# Revit family: 1000_Sliding_Window_XX_Standard
name_source: partatom
category: Windows
revit_build: Autodesk Revit 2014 (Build: 20130308_1515(x64)
units: mm (PartAtom-declared; Revit-internal decimal feet)

## types (117) — shared parameters
Centered In Wall = Yes
Default Sill Height = 800 mm
Description = Sliding window, XX
Equal Sash Width = Yes
Frame Thickness = 76 mm
Limit Sash Height Max = 1800 mm  [stored 5.90551 ft]
Limit Sash Height Min = 300 mm
Limit Sash Width Max = 1500 mm  [stored 4.92126 ft]
Limit Sash Width Min = 300 mm
Limit Window Height Max = 1857 mm
Limit Window Height Min = 357 mm
Limit Window Width Max = 2999 mm
Limit Window Width Min = 599 mm
Manufacturer = Crealco
Model = 1000
Sash Frame Seal = 2 mm  [stored 0.00656168 ft]
URL = http://www.crealco.co.za
Wall Closure = By host
zero-valued in all types: Custom Frame Offset From Exterior, Custom Sash Width Left

## per-type parameters (varying)
- 1000SW-0906XX-1000Pa: Area Left Sash Glazing=0.15 m²; Area Right Sash Glazing=0.15 m²; Clearvue SHGC Value=0.536; Clearvue U Value=5.91; Custom Windload=1000 mm  [stored 3.28084 ft]; Custom Window Height=590 mm  [stored 1.9357 ft]; Custom Window Width=890 mm  [stored 2.91995 ft]; Energy Advantage SHGC Value=0.481; Energy Advantage U Value=4.85; Heavy Duty Interlocker=No; Height=590 mm  [stored 1.9357 ft]; Intruderprufe LowE SHGC Value=0.444; Intruderprufe LowE U Value=4.814; Intruderprufe SHGC Value=0.509; Intruderprufe U Value=5.8; Is Heavy Duty Mullion=0 mm  [stored 0 ft]; Limit Sash Width Left Max=591 mm; Limit Sash Width Left Min=300 mm; Max Pane Area=0.15 m²; Sash Height=533 mm; Sash Width Left=446 mm; Sash Width Right=446 mm; Standard Interlocker=Yes; Width=890 mm  [stored 2.91995 ft]; Windload Design=1000 mm  [stored 3.28084 ft]
- 1000SW-1206XX-1000Pa: Area Left Sash Glazing=0.21 m²; Area Right Sash Glazing=0.21 m²; Clearvue SHGC Value=0.627; Clearvue U Value=5.85; Custom Windload=1000 mm  [stored 3.28084 ft]; Custom Window Height=590 mm  [stored 1.9357 ft]; Custom Window Width=1190 mm  [stored 3.9042 ft]; Energy Advantage SHGC Value=0.562; Energy Advantage U Value=4.52; Heavy Duty Interlocker=No; Height=590 mm  [stored 1.9357 ft]; Intruderprufe LowE SHGC Value=0.525; Intruderprufe LowE U Value=4.47; Intruderprufe SHGC Value=0.595; Intruderprufe U Value=5.91; Is Heavy Duty Mullion=0 mm  [stored 0 ft]; Limit Sash Width Left Max=891 mm; Limit Sash Width Left Min=300 mm; Max Pane Area=0.21 m²; Sash Height=533 mm; Sash Width Left=596 mm; Sash Width Right=596 mm; Standard Interlocker=Yes; Width=1190 mm  [stored 3.9042 ft]; Windload Design=1000 mm  [stored 3.28084 ft]
- 1000SW-1506XX-1000Pa: Area Left Sash Glazing=0.28 m²; Area Right Sash Glazing=0.28 m²; Clearvue SHGC Value=0.568; Clearvue U Value=6.09; Custom Windload=1000 mm  [stored 3.28084 ft]; Custom Window Height=590 mm  [stored 1.9357 ft]; Custom Window Width=1490 mm  [stored 4.88845 ft]; Energy Advantage SHGC Value=0.509; Energy Advantage U Value=4.84; Heavy Duty Interlocker=No; Height=590 mm  [stored 1.9357 ft]; Intruderprufe LowE SHGC Value=0.459; Intruderprufe LowE U Value=4.81; Intruderprufe SHGC Value=0.539; Intruderprufe U Value=5.98; Is Heavy Duty Mullion=0 mm  [stored 0 ft]; Limit Sash Width Left Max=1191 mm; Limit Sash Width Left Min=300 mm; Max Pane Area=0.28 m²; Sash Height=533 mm; Sash Width Left=746 mm; Sash Width Right=746 mm; Standard Interlocker=Yes; Width=1490 mm  [stored 4.88845 ft]; Windload Design=1000 mm  [stored 3.28084 ft]
- 1000SW-1806XX-1000Pa: Area Left Sash Glazing=0.34 m²; Area Right Sash Glazing=0.34 m²; Clearvue SHGC Value=0.576; Clearvue U Value=6.14; Custom Windload=1000 mm  [stored 3.28084 ft]; Custom Window Height=590 mm  [stored 1.9357 ft]; Custom Window Width=1790 mm  [stored 5.8727 ft]; Energy Advantage SHGC Value=0.516; Energy Advantage U Value=4.84; Heavy Duty Interlocker=No; Height=590 mm  [stored 1.9357 ft]; Intruderprufe LowE SHGC Value=0.476; Intruderprufe LowE U Value=4.81; Intruderprufe SHGC Value=0.547; Intruderprufe U Value=6.02; Is Heavy Duty Mullion=0 mm  [stored 0 ft]; Limit Sash Width Left Max=1491 mm; Limit Sash Width Left Min=300 mm; Max Pane Area=0.34 m²; Sash Height=533 mm; Sash Width Left=896 mm; Sash Width Right=896 mm; Standard Interlocker=Yes; Width=1790 mm  [stored 5.8727 ft]; Windload Design=1000 mm  [stored 3.28084 ft]
- 1000SW-2106XX-1000Pa: Area Left Sash Glazing=0.41 m²; Area Right Sash Glazing=0.41 m²; Clearvue SHGC Value=0.581; Clearvue U Value=6.17; Custom Windload=1000 mm  [stored 3.28084 ft]; Custom Window Height=590 mm  [stored 1.9357 ft]; Custom Window Width=2090 mm  [stored 6.85696 ft]; Energy Advantage SHGC Value=0.521; Energy Advantage U Value=4.84; Heavy Duty Interlocker=No; Height=590 mm  [stored 1.9357 ft]; Intruderprufe LowE SHGC Value=0.48; Intruderprufe LowE U Value=4.8; Intruderprufe SHGC Value=0.552; Intruderprufe U Value=6.05; Is Heavy Duty Mullion=0 mm  [stored 0 ft]; Limit Sash Width Left Max=1500 mm  [stored 4.92126 ft]; Limit Sash Width Left Min=591 mm; Max Pane Area=0.41 m²; Sash Height=533 mm; Sash Width Left=1046 mm; Sash Width Right=1046 mm; Standard Interlocker=Yes; Width=2090 mm  [stored 6.85696 ft]; Windload Design=1000 mm  [stored 3.28084 ft]
- 1000SW-2406XX-1000Pa: Area Left Sash Glazing=0.47 m²; Area Right Sash Glazing=0.47 m²; Clearvue SHGC Value=0.586; Clearvue U Value=6.19; Custom Windload=1000 mm  [stored 3.28084 ft]; Custom Window Height=590 mm  [stored 1.9357 ft]; Custom Window Width=2390 mm  [stored 7.84121 ft]; Energy Advantage SHGC Value=0.525; Energy Advantage U Value=4.84; Heavy Duty Interlocker=No; Height=590 mm  [stored 1.9357 ft]; Intruderprufe LowE SHGC Value=0.484; Intruderprufe LowE U Value=4.8; Intruderprufe SHGC Value=0.556; Intruderprufe U Value=6.08; Is Heavy Duty Mullion=0 mm  [stored 0 ft]; Limit Sash Width Left Max=1500 mm  [stored 4.92126 ft]; Limit Sash Width Left Min=891 mm; Max Pane Area=0.47 m²; Sash Height=533 mm; Sash Width Left=1196 mm; Sash Width Right=1196 mm; Standard Interlocker=Yes; Width=2390 mm  [stored 7.84121 ft]; Windload Design=1000 mm  [stored 3.28084 ft]
- 1000SW-2706XX-1000Pa: Area Left Sash Glazing=0.54 m²; Area Right Sash Glazing=0.54 m²; Clearvue SHGC Value=0.589; Clearvue U Value=6.21; Custom Windload=1000 mm  [stored 3.28084 ft]; Custom Window Height=590 mm  [stored 1.9357 ft]; Custom Window Width=2690 mm; Energy Advantage SHGC Value=0.528; Energy Advantage U Value=4.84; Heavy Duty Interlocker=No; Height=590 mm  [stored 1.9357 ft]; Intruderprufe LowE SHGC Value=0.486; Intruderprufe LowE U Value=4.8; Intruderprufe SHGC Value=0.559; Intruderprufe U Value=6.09; Is Heavy Duty Mullion=0 mm  [stored 0 ft]; Limit Sash Width Left Max=1500 mm  [stored 4.92126 ft]; Limit Sash Width Left Min=1191 mm; Max Pane Area=0.54 m²; Sash Height=533 mm; Sash Width Left=1346 mm; Sash Width Right=1346 mm; Standard Interlocker=Yes; Width=2690 mm; Windload Design=1000 mm  [stored 3.28084 ft]
- 1000SW-3006XX-1000Pa: Area Left Sash Glazing=0.6 m²; Area Right Sash Glazing=0.6 m²; Clearvue SHGC Value=0.592; Clearvue U Value=6.22; Custom Windload=1000 mm  [stored 3.28084 ft]; Custom Window Height=590 mm  [stored 1.9357 ft]; Custom Window Width=2990 mm  [stored 9.80971 ft]; Energy Advantage SHGC Value=0.53; Energy Advantage U Value=4.84; Heavy Duty Interlocker=No; Height=590 mm  [stored 1.9357 ft]; Intruderprufe LowE SHGC Value=0.488; Intruderprufe LowE U Value=4.8; Intruderprufe SHGC Value=0.562; Intruderprufe U Value=6.11; Is Heavy Duty Mullion=0 mm  [stored 0 ft]; Limit Sash Width Left Max=1500 mm  [stored 4.92126 ft]; Limit Sash Width Left Min=1491 mm; Max Pane Area=0.6 m²; Sash Height=533 mm; Sash Width Left=1496 mm; Sash Width Right=1496 mm; Standard Interlocker=Yes; Width=2990 mm  [stored 9.80971 ft]; Windload Design=1000 mm  [stored 3.28084 ft]
- 1000SW-0909XX-1000Pa: Area Left Sash Glazing=0.25 m²; Area Right Sash Glazing=0.25 m²; Clearvue SHGC Value=0.604; Clearvue U Value=5.73; Custom Windload=1000 mm  [stored 3.28084 ft]; Custom Window Height=890 mm  [stored 2.91995 ft]; Custom Window Width=890 mm  [stored 2.91995 ft]; Energy Advantage SHGC Value=0.541; Energy Advantage U Value=4.54; Heavy Duty Interlocker=No; Height=890 mm  [stored 2.91995 ft]; Intruderprufe LowE SHGC Value=0.502; Intruderprufe LowE U Value=4.49; Intruderprufe SHGC Value=0.574; Intruderprufe U Value=5.63; Is Heavy Duty Mullion=0 mm  [stored 0 ft]; Limit Sash Width Left Max=591 mm; Limit Sash Width Left Min=300 mm; Max Pane Area=0.25 m²; Sash Height=833 mm; Sash Width Left=446 mm; Sash Width Right=446 mm; Standard Interlocker=Yes; Width=890 mm  [stored 2.91995 ft]; Windload Design=1000 mm  [stored 3.28084 ft]
- 1000SW-1209XX-1000Pa: Area Left Sash Glazing=0.36 m²; Area Right Sash Glazing=0.36 m²; Clearvue SHGC Value=0.627; Clearvue U Value=5.85; Custom Windload=1000 mm  [stored 3.28084 ft]; Custom Window Height=890 mm  [stored 2.91995 ft]; Custom Window Width=1190 mm  [stored 3.9042 ft]; Energy Advantage SHGC Value=0.562; Energy Advantage U Value=4.52; Heavy Duty Interlocker=No; Height=890 mm  [stored 2.91995 ft]; Intruderprufe LowE SHGC Value=0.52; Intruderprufe LowE U Value=4.47; Intruderprufe SHGC Value=0.595; Intruderprufe U Value=5.74; Is Heavy Duty Mullion=0 mm  [stored 0 ft]; Limit Sash Width Left Max=891 mm; Limit Sash Width Left Min=300 mm; Max Pane Area=0.36 m²; Sash Height=833 mm; Sash Width Left=596 mm; Sash Width Right=596 mm; Standard Interlocker=Yes; Width=1190 mm  [stored 3.9042 ft]; Windload Design=1000 mm  [stored 3.28084 ft]
- 1000SW-1509XX-1000Pa: Area Left Sash Glazing=0.47 m²; Area Right Sash Glazing=0.47 m²; Clearvue SHGC Value=0.641; Clearvue U Value=5.92; Custom Windload=1000 mm  [stored 3.28084 ft]; Custom Window Height=890 mm  [stored 2.91995 ft]; Custom Window Width=1490 mm  [stored 4.88845 ft]; Energy Advantage SHGC Value=0.573; Energy Advantage U Value=4.5; Heavy Duty Interlocker=No; Height=890 mm  [stored 2.91995 ft]; Intruderprufe LowE SHGC Value=0.531; Intruderprufe LowE U Value=4.45; Intruderprufe SHGC Value=0.608; Intruderprufe U Value=5.81; Is Heavy Duty Mullion=0 mm  [stored 0 ft]; Limit Sash Width Left Max=1191 mm; Limit Sash Width Left Min=300 mm; Max Pane Area=0.47 m²; Sash Height=833 mm; Sash Width Left=746 mm; Sash Width Right=746 mm; Standard Interlocker=Yes; Width=1490 mm  [stored 4.88845 ft]; Windload Design=1000 mm  [stored 3.28084 ft]
- 1000SW-1809XX-1000Pa: Area Left Sash Glazing=0.58 m²; Area Right Sash Glazing=0.58 m²; Clearvue SHGC Value=0.65; Clearvue U Value=5.97; Custom Windload=1000 mm  [stored 3.28084 ft]; Custom Window Height=890 mm  [stored 2.91995 ft]; Custom Window Width=1790 mm  [stored 5.8727 ft]; Energy Advantage SHGC Value=0.581; Energy Advantage U Value=4.5; Heavy Duty Interlocker=No; Height=890 mm  [stored 2.91995 ft]; Intruderprufe LowE SHGC Value=0.538; Intruderprufe LowE U Value=4.45; Intruderprufe SHGC Value=0.617; Intruderprufe U Value=5.85; Is Heavy Duty Mullion=0 mm  [stored 0 ft]; Limit Sash Width Left Max=1491 mm; Limit Sash Width Left Min=300 mm; Max Pane Area=0.58 m²; Sash Height=833 mm; Sash Width Left=896 mm; Sash Width Right=896 mm; Standard Interlocker=Yes; Width=1790 mm  [stored 5.8727 ft]; Windload Design=1000 mm  [stored 3.28084 ft]
- 1000SW-2109XX-1000Pa: Area Left Sash Glazing=0.69 m²; Area Right Sash Glazing=0.69 m²; Clearvue SHGC Value=0.656; Clearvue U Value=6; Custom Windload=1000 mm  [stored 3.28084 ft]; Custom Window Height=890 mm  [stored 2.91995 ft]; Custom Window Width=2090 mm  [stored 6.85696 ft]; Energy Advantage SHGC Value=0.587; Energy Advantage U Value=4.49; Heavy Duty Interlocker=No; Height=890 mm  [stored 2.91995 ft]; Intruderprufe LowE SHGC Value=0.543; Intruderprufe LowE U Value=4.44; Intruderprufe SHGC Value=0.623; Intruderprufe U Value=5.88; Is Heavy Duty Mullion=0 mm  [stored 0 ft]; Limit Sash Width Left Max=1500 mm  [stored 4.92126 ft]; Limit Sash Width Left Min=591 mm; Max Pane Area=0.69 m²; Sash Height=833 mm; Sash Width Left=1046 mm; Sash Width Right=1046 mm; Standard Interlocker=Yes; Width=2090 mm  [stored 6.85696 ft]; Windload Design=1000 mm  [stored 3.28084 ft]
- 1000SW-2409XX-1000Pa: Area Left Sash Glazing=0.8 m²; Area Right Sash Glazing=0.8 m²; Clearvue SHGC Value=0.661; Clearvue U Value=6.02; Custom Windload=1000 mm  [stored 3.28084 ft]; Custom Window Height=890 mm  [stored 2.91995 ft]; Custom Window Width=2390 mm  [stored 7.84121 ft]; Energy Advantage SHGC Value=0.591; Energy Advantage U Value=4.48; Heavy Duty Interlocker=No; Height=890 mm  [stored 2.91995 ft]; Intruderprufe LowE SHGC Value=0.547; Intruderprufe LowE U Value=4.44; Intruderprufe SHGC Value=0.627; Intruderprufe U Value=5.91; Is Heavy Duty Mullion=0 mm  [stored 0 ft]; Limit Sash Width Left Max=1500 mm  [stored 4.92126 ft]; Limit Sash Width Left Min=891 mm; Max Pane Area=0.8 m²; Sash Height=833 mm; Sash Width Left=1196 mm; Sash Width Right=1196 mm; Standard Interlocker=Yes; Width=2390 mm  [stored 7.84121 ft]; Windload Design=1000 mm  [stored 3.28084 ft]
- 1000SW-2709XX-1000Pa: Area Left Sash Glazing=0.91 m²; Area Right Sash Glazing=0.91 m²; Clearvue SHGC Value=0.665; Clearvue U Value=6.04; Custom Windload=1000 mm  [stored 3.28084 ft]; Custom Window Height=890 mm  [stored 2.91995 ft]; Custom Window Width=2690 mm; Energy Advantage SHGC Value=0.595; Energy Advantage U Value=4.48; Heavy Duty Interlocker=No; Height=890 mm  [stored 2.91995 ft]; Intruderprufe LowE SHGC Value=0.55; Intruderprufe LowE U Value=4.43; Intruderprufe SHGC Value=0.631; Intruderprufe U Value=5.92; Is Heavy Duty Mullion=0 mm  [stored 0 ft]; Limit Sash Width Left Max=1500 mm  [stored 4.92126 ft]; Limit Sash Width Left Min=1191 mm; Max Pane Area=0.91 m²; Sash Height=833 mm; Sash Width Left=1346 mm; Sash Width Right=1346 mm; Standard Interlocker=Yes; Width=2690 mm; Windload Design=1000 mm  [stored 3.28084 ft]
- 1000SW-3009XX-1000Pa: Area Left Sash Glazing=1.02 m²; Area Right Sash Glazing=1.02 m²; Clearvue SHGC Value=0.668; Clearvue U Value=6.06; Custom Windload=1000 mm  [stored 3.28084 ft]; Custom Window Height=890 mm  [stored 2.91995 ft]; Custom Window Width=2990 mm  [stored 9.80971 ft]; Energy Advantage SHGC Value=0.597; Energy Advantage U Value=4.48; Heavy Duty Interlocker=No; Height=890 mm  [stored 2.91995 ft]; Intruderprufe LowE SHGC Value=0.552; Intruderprufe LowE U Value=4.43; Intruderprufe SHGC Value=0.634; Intruderprufe U Value=5.94; Is Heavy Duty Mullion=0 mm  [stored 0 ft]; Limit Sash Width Left Max=1500 mm  [stored 4.92126 ft]; Limit Sash Width Left Min=1491 mm; Max Pane Area=1.02 m²; Sash Height=833 mm; Sash Width Left=1496 mm; Sash Width Right=1496 mm; Standard Interlocker=Yes; Width=2990 mm  [stored 9.80971 ft]; Windload Design=1000 mm  [stored 3.28084 ft]
- 1000SW-0912XX-1000Pa: Area Left Sash Glazing=0.36 m²; Area Right Sash Glazing=0.36 m²; Clearvue SHGC Value=2.638; Clearvue U Value=5.65; Custom Windload=1000 mm  [stored 3.28084 ft]; Custom Window Height=1190 mm  [stored 3.9042 ft]; Custom Window Width=890 mm  [stored 2.91995 ft]; Energy Advantage SHGC Value=0.572; Energy Advantage U Value=4.39; Heavy Duty Interlocker=No; Height=1190 mm  [stored 3.9042 ft]; Intruderprufe LowE SHGC Value=0.531; Intruderprufe LowE U Value=4.33; Intruderprufe SHGC Value=0.606; Intruderprufe U Value=5.54; Is Heavy Duty Mullion=0 mm  [stored 0 ft]; Limit Sash Width Left Max=591 mm; Limit Sash Width Left Min=300 mm; Max Pane Area=0.36 m²; Sash Height=1133 mm; Sash Width Left=446 mm; Sash Width Right=446 mm; Standard Interlocker=Yes; Width=890 mm  [stored 2.91995 ft]; Windload Design=1000 mm  [stored 3.28084 ft]
- 1000SW-1212XX-1000Pa: Area Left Sash Glazing=0.51 m²; Area Right Sash Glazing=0.51 m²; Clearvue SHGC Value=0.662; Clearvue U Value=5.77; Custom Windload=1000 mm  [stored 3.28084 ft]; Custom Window Height=1190 mm  [stored 3.9042 ft]; Custom Window Width=1190 mm  [stored 3.9042 ft]; Energy Advantage SHGC Value=0.593; Energy Advantage U Value=4.35; Heavy Duty Interlocker=No; Height=1190 mm  [stored 3.9042 ft]; Intruderprufe LowE SHGC Value=0.55; Intruderprufe LowE U Value=4.3; Intruderprufe SHGC Value=0.629; Intruderprufe U Value=5.65; Is Heavy Duty Mullion=0 mm  [stored 0 ft]; Limit Sash Width Left Max=891 mm; Limit Sash Width Left Min=300 mm; Max Pane Area=0.51 m²; Sash Height=1133 mm; Sash Width Left=596 mm; Sash Width Right=596 mm; Standard Interlocker=Yes; Width=1190 mm  [stored 3.9042 ft]; Windload Design=1000 mm  [stored 3.28084 ft]
- 1000SW-1512XX-1000Pa: Area Left Sash Glazing=0.67 m²; Area Right Sash Glazing=0.67 m²; Clearvue SHGC Value=0.677; Clearvue U Value=5.84; Custom Windload=1000 mm  [stored 3.28084 ft]; Custom Window Height=1190 mm  [stored 3.9042 ft]; Custom Window Width=1490 mm  [stored 4.88845 ft]; Energy Advantage SHGC Value=0.605; Energy Advantage U Value=4.34; Heavy Duty Interlocker=No; Height=1190 mm  [stored 3.9042 ft]; Intruderprufe LowE SHGC Value=0.561; Intruderprufe LowE U Value=4.28; Intruderprufe SHGC Value=0.642; Intruderprufe U Value=5.72; Is Heavy Duty Mullion=0 mm  [stored 0 ft]; Limit Sash Width Left Max=1191 mm; Limit Sash Width Left Min=300 mm; Max Pane Area=0.67 m²; Sash Height=1133 mm; Sash Width Left=746 mm; Sash Width Right=746 mm; Standard Interlocker=Yes; Width=1490 mm  [stored 4.88845 ft]; Windload Design=1000 mm  [stored 3.28084 ft]
- 1000SW-1812XX-1000Pa: Area Left Sash Glazing=0.82 m²; Area Right Sash Glazing=0.82 m²; Clearvue SHGC Value=0.686; Clearvue U Value=5.88; Custom Windload=1000 mm  [stored 3.28084 ft]; Custom Window Height=1190 mm  [stored 3.9042 ft]; Custom Window Width=1790 mm  [stored 5.8727 ft]; Energy Advantage SHGC Value=0.614; Energy Advantage U Value=4.32; Heavy Duty Interlocker=No; Height=1190 mm  [stored 3.9042 ft]; Intruderprufe LowE SHGC Value=0.569; Intruderprufe LowE U Value=4.27; Intruderprufe SHGC Value=0.651; Intruderprufe U Value=5.77; Is Heavy Duty Mullion=0 mm  [stored 0 ft]; Limit Sash Width Left Max=1491 mm; Limit Sash Width Left Min=300 mm; Max Pane Area=0.82 m²; Sash Height=1133 mm; Sash Width Left=896 mm; Sash Width Right=896 mm; Standard Interlocker=Yes; Width=1790 mm  [stored 5.8727 ft]; Windload Design=1000 mm  [stored 3.28084 ft]
- 1000SW-2112XX-1000Pa: Area Left Sash Glazing=0.98 m²; Area Right Sash Glazing=0.98 m²; Clearvue SHGC Value=0.693; Clearvue U Value=5.92; Custom Windload=1000 mm  [stored 3.28084 ft]; Custom Window Height=1190 mm  [stored 3.9042 ft]; Custom Window Width=2090 mm  [stored 6.85696 ft]; Energy Advantage SHGC Value=0.62; Energy Advantage U Value=4.32; Heavy Duty Interlocker=No; Height=1190 mm  [stored 3.9042 ft]; Intruderprufe LowE SHGC Value=0.574; Intruderprufe LowE U Value=4.26; Intruderprufe SHGC Value=0.658; Intruderprufe U Value=5.8; Is Heavy Duty Mullion=0 mm  [stored 0 ft]; Limit Sash Width Left Max=1500 mm  [stored 4.92126 ft]; Limit Sash Width Left Min=591 mm; Max Pane Area=0.98 m²; Sash Height=1133 mm; Sash Width Left=1046 mm; Sash Width Right=1046 mm; Standard Interlocker=Yes; Width=2090 mm  [stored 6.85696 ft]; Windload Design=1000 mm  [stored 3.28084 ft]
- 1000SW-2412XX-1000Pa: Area Left Sash Glazing=1.13 m²; Area Right Sash Glazing=1.13 m²; Clearvue SHGC Value=0.698; Clearvue U Value=5.94; Custom Windload=1000 mm  [stored 3.28084 ft]; Custom Window Height=1190 mm  [stored 3.9042 ft]; Custom Window Width=2390 mm  [stored 7.84121 ft]; Energy Advantage SHGC Value=0.624; Energy Advantage U Value=4.31; Heavy Duty Interlocker=No; Height=1190 mm  [stored 3.9042 ft]; Intruderprufe LowE SHGC Value=0.578; Intruderprufe LowE U Value=4.26; Intruderprufe SHGC Value=0.663; Intruderprufe U Value=5.82; Is Heavy Duty Mullion=0 mm  [stored 0 ft]; Limit Sash Width Left Max=1500 mm  [stored 4.92126 ft]; Limit Sash Width Left Min=891 mm; Max Pane Area=1.13 m²; Sash Height=1133 mm; Sash Width Left=1196 mm; Sash Width Right=1196 mm; Standard Interlocker=Yes; Width=2390 mm  [stored 7.84121 ft]; Windload Design=1000 mm  [stored 3.28084 ft]
- 1000SW-2712XX-1000Pa: Area Left Sash Glazing=1.28 m²; Area Right Sash Glazing=1.28 m²; Clearvue SHGC Value=0.702; Clearvue U Value=5.96; Custom Windload=1000 mm  [stored 3.28084 ft]; Custom Window Height=1190 mm  [stored 3.9042 ft]; Custom Window Width=2690 mm; Energy Advantage SHGC Value=0.628; Energy Advantage U Value=4.3; Heavy Duty Interlocker=No; Height=1190 mm  [stored 3.9042 ft]; Intruderprufe LowE SHGC Value=0.582; Intruderprufe LowE U Value=4.25; Intruderprufe SHGC Value=0.666; Intruderprufe U Value=5.84; Is Heavy Duty Mullion=0 mm  [stored 0 ft]; Limit Sash Width Left Max=1500 mm  [stored 4.92126 ft]; Limit Sash Width Left Min=1191 mm; Max Pane Area=1.28 m²; Sash Height=1133 mm; Sash Width Left=1346 mm; Sash Width Right=1346 mm; Standard Interlocker=Yes; Width=2690 mm; Windload Design=1000 mm  [stored 3.28084 ft]
- 1000SW-3012XX-1000Pa: Area Left Sash Glazing=1.44 m²; Area Right Sash Glazing=1.44 m²; Clearvue SHGC Value=0.705; Clearvue U Value=5.98; Custom Windload=1000 mm  [stored 3.28084 ft]; Custom Window Height=1190 mm  [stored 3.9042 ft]; Custom Window Width=2990 mm  [stored 9.80971 ft]; Energy Advantage SHGC Value=0.631; Energy Advantage U Value=4.3; Heavy Duty Interlocker=No; Height=1190 mm  [stored 3.9042 ft]; Intruderprufe LowE SHGC Value=0.584; Intruderprufe LowE U Value=4.25; Intruderprufe SHGC Value=0.669; Intruderprufe U Value=5.86; Is Heavy Duty Mullion=0 mm  [stored 0 ft]; Limit Sash Width Left Max=1500 mm  [stored 4.92126 ft]; Limit Sash Width Left Min=1491 mm; Max Pane Area=1.44 m²; Sash Height=1133 mm; Sash Width Left=1496 mm; Sash Width Right=1496 mm; Standard Interlocker=Yes; Width=2990 mm  [stored 9.80971 ft]; Windload Design=1000 mm  [stored 3.28084 ft]
- 1000SW-0915XX-1000Pa: Area Left Sash Glazing=0.46 m²; Area Right Sash Glazing=0.46 m²; Clearvue SHGC Value=0.658; Clearvue U Value=5.6; Custom Windload=1000 mm  [stored 3.28084 ft]; Custom Window Height=1490 mm  [stored 4.88845 ft]; Custom Window Width=890 mm  [stored 2.91995 ft]; Energy Advantage SHGC Value=0.59; Energy Advantage U Value=4.29; Heavy Duty Interlocker=No; Height=1490 mm  [stored 4.88845 ft]; Intruderprufe LowE SHGC Value=0.548; Intruderprufe LowE U Value=4.23; Intruderprufe SHGC Value=0.625; Intruderprufe U Value=5.49; Is Heavy Duty Mullion=0 mm  [stored 0 ft]; Limit Sash Width Left Max=591 mm; Limit Sash Width Left Min=300 mm; Max Pane Area=0.46 m²; Sash Height=1433 mm; Sash Width Left=446 mm; Sash Width Right=446 mm; Standard Interlocker=Yes; Width=890 mm  [stored 2.91995 ft]; Windload Design=1000 mm  [stored 3.28084 ft]
- 1000SW-1215XX-1000Pa: Area Left Sash Glazing=0.66 m²; Area Right Sash Glazing=0.66 m²; Clearvue SHGC Value=0.683; Clearvue U Value=5.72; Custom Windload=1000 mm  [stored 3.28084 ft]; Custom Window Height=1490 mm  [stored 4.88845 ft]; Custom Window Width=1190 mm  [stored 3.9042 ft]; Energy Advantage SHGC Value=0.611; Energy Advantage U Value=4.26; Heavy Duty Interlocker=No; Height=1490 mm  [stored 4.88845 ft]; Intruderprufe LowE SHGC Value=0.568; Intruderprufe LowE U Value=4.2; Intruderprufe SHGC Value=0.649; Intruderprufe U Value=5.6; Is Heavy Duty Mullion=0 mm  [stored 0 ft]; Limit Sash Width Left Max=891 mm; Limit Sash Width Left Min=300 mm; Max Pane Area=0.66 m²; Sash Height=1433 mm; Sash Width Left=596 mm; Sash Width Right=596 mm; Standard Interlocker=Yes; Width=1190 mm  [stored 3.9042 ft]; Windload Design=1000 mm  [stored 3.28084 ft]
- 1000SW-1515XX-1000Pa: Area Left Sash Glazing=0.86 m²; Area Right Sash Glazing=0.86 m²; Clearvue SHGC Value=0.698; Clearvue U Value=5.79; Custom Windload=1000 mm  [stored 3.28084 ft]; Custom Window Height=1490 mm  [stored 4.88845 ft]; Custom Window Width=1490 mm  [stored 4.88845 ft]; Energy Advantage SHGC Value=0.625; Energy Advantage U Value=4.24; Heavy Duty Interlocker=No; Height=1490 mm  [stored 4.88845 ft]; Intruderprufe LowE SHGC Value=0.58; Intruderprufe LowE U Value=4.18; Intruderprufe SHGC Value=0.663; Intruderprufe U Value=5.67; Is Heavy Duty Mullion=0 mm  [stored 0 ft]; Limit Sash Width Left Max=1191 mm; Limit Sash Width Left Min=300 mm; Max Pane Area=0.86 m²; Sash Height=1433 mm; Sash Width Left=746 mm; Sash Width Right=746 mm; Standard Interlocker=Yes; Width=1490 mm  [stored 4.88845 ft]; Windload Design=1000 mm  [stored 3.28084 ft]
- 1000SW-1815XX-1000Pa: Area Left Sash Glazing=1.06 m²; Area Right Sash Glazing=1.06 m²; Clearvue SHGC Value=0.708; Clearvue U Value=5.83; Custom Windload=1000 mm  [stored 3.28084 ft]; Custom Window Height=1490 mm  [stored 4.88845 ft]; Custom Window Width=1790 mm  [stored 5.8727 ft]; Energy Advantage SHGC Value=0.633; Energy Advantage U Value=4.22; Heavy Duty Interlocker=No; Height=1490 mm  [stored 4.88845 ft]; Intruderprufe LowE SHGC Value=0.587; Intruderprufe LowE U Value=4.16; Intruderprufe SHGC Value=0.672; Intruderprufe U Value=5.72; Is Heavy Duty Mullion=0 mm  [stored 0 ft]; Limit Sash Width Left Max=1491 mm; Limit Sash Width Left Min=300 mm; Max Pane Area=1.06 m²; Sash Height=1433 mm; Sash Width Left=896 mm; Sash Width Right=896 mm; Standard Interlocker=Yes; Width=1790 mm  [stored 5.8727 ft]; Windload Design=1000 mm  [stored 3.28084 ft]
- 1000SW-2115XX-1000Pa: Area Left Sash Glazing=1.26 m²; Area Right Sash Glazing=1.26 m²; Clearvue SHGC Value=0.715; Clearvue U Value=5.87; Custom Windload=1000 mm  [stored 3.28084 ft]; Custom Window Height=1490 mm  [stored 4.88845 ft]; Custom Window Width=2090 mm  [stored 6.85696 ft]; Energy Advantage SHGC Value=0.639; Energy Advantage U Value=4.21; Heavy Duty Interlocker=No; Height=1490 mm  [stored 4.88845 ft]; Intruderprufe LowE SHGC Value=0.595; Intruderprufe LowE U Value=4.15; Intruderprufe SHGC Value=0.679; Intruderprufe U Value=5.75; Is Heavy Duty Mullion=0 mm  [stored 0 ft]; Limit Sash Width Left Max=1500 mm  [stored 4.92126 ft]; Limit Sash Width Left Min=591 mm; Max Pane Area=1.26 m²; Sash Height=1433 mm; Sash Width Left=1046 mm; Sash Width Right=1046 mm; Standard Interlocker=Yes; Width=2090 mm  [stored 6.85696 ft]; Windload Design=1000 mm  [stored 3.28084 ft]
- 1000SW-2415XX-1000Pa: Area Left Sash Glazing=1.46 m²; Area Right Sash Glazing=1.46 m²; Clearvue SHGC Value=0.721; Clearvue U Value=5.89; Custom Windload=1000 mm  [stored 3.28084 ft]; Custom Window Height=1490 mm  [stored 4.88845 ft]; Custom Window Width=2390 mm  [stored 7.84121 ft]; Energy Advantage SHGC Value=0.644; Energy Advantage U Value=4.2; Heavy Duty Interlocker=No; Height=1490 mm  [stored 4.88845 ft]; Intruderprufe LowE SHGC Value=0.597; Intruderprufe LowE U Value=4.15; Intruderprufe SHGC Value=0.684; Intruderprufe U Value=5.77; Is Heavy Duty Mullion=0 mm  [stored 0 ft]; Limit Sash Width Left Max=1500 mm  [stored 4.92126 ft]; Limit Sash Width Left Min=891 mm; Max Pane Area=1.46 m²; Sash Height=1433 mm; Sash Width Left=1196 mm; Sash Width Right=1196 mm; Standard Interlocker=Yes; Width=2390 mm  [stored 7.84121 ft]; Windload Design=1000 mm  [stored 3.28084 ft]
- 1000SW-2715XX-1000Pa: Area Left Sash Glazing=1.66 m²; Area Right Sash Glazing=1.66 m²; Clearvue SHGC Value=0.725; Clearvue U Value=5.91; Custom Windload=1000 mm  [stored 3.28084 ft]; Custom Window Height=1490 mm  [stored 4.88845 ft]; Custom Window Width=2690 mm; Energy Advantage SHGC Value=0.648; Energy Advantage U Value=4.2; Heavy Duty Interlocker=No; Height=1490 mm  [stored 4.88845 ft]; Intruderprufe LowE SHGC Value=0.601; Intruderprufe LowE U Value=4.14; Intruderprufe SHGC Value=0.687; Intruderprufe U Value=5.79; Is Heavy Duty Mullion=0 mm  [stored 0 ft]; Limit Sash Width Left Max=1500 mm  [stored 4.92126 ft]; Limit Sash Width Left Min=1191 mm; Max Pane Area=1.66 m²; Sash Height=1433 mm; Sash Width Left=1346 mm; Sash Width Right=1346 mm; Standard Interlocker=Yes; Width=2690 mm; Windload Design=1000 mm  [stored 3.28084 ft]
- 1000SW-3015XX-1000Pa: Area Left Sash Glazing=1.86 m²; Area Right Sash Glazing=1.86 m²; Clearvue SHGC Value=0.728; Clearvue U Value=5.93; Custom Windload=1000 mm  [stored 3.28084 ft]; Custom Window Height=1490 mm  [stored 4.88845 ft]; Custom Window Width=2990 mm  [stored 9.80971 ft]; Energy Advantage SHGC Value=0.651; Energy Advantage U Value=4.19; Heavy Duty Interlocker=No; Height=1490 mm  [stored 4.88845 ft]; Intruderprufe LowE SHGC Value=0.603; Intruderprufe LowE U Value=4.14; Intruderprufe SHGC Value=0.691; Intruderprufe U Value=5.81; Is Heavy Duty Mullion=0 mm  [stored 0 ft]; Limit Sash Width Left Max=1500 mm  [stored 4.92126 ft]; Limit Sash Width Left Min=1491 mm; Max Pane Area=1.86 m²; Sash Height=1433 mm; Sash Width Left=1496 mm; Sash Width Right=1496 mm; Standard Interlocker=Yes; Width=2990 mm  [stored 9.80971 ft]; Windload Design=1000 mm  [stored 3.28084 ft]
- 1000SW-1218XX-1000Pa: Area Left Sash Glazing=0.81 m²; Area Right Sash Glazing=0.81 m²; Clearvue SHGC Value=0.697; Clearvue U Value=5.68; Custom Windload=1000 mm  [stored 3.28084 ft]; Custom Window Height=1790 mm  [stored 5.8727 ft]; Custom Window Width=1190 mm  [stored 3.9042 ft]; Energy Advantage SHGC Value=0.624; Energy Advantage U Value=4.19; Heavy Duty Interlocker=No; Height=1790 mm  [stored 5.8727 ft]; Intruderprufe LowE SHGC Value=0.579; Intruderprufe LowE U Value=4.13; Intruderprufe SHGC Value=0.662; Intruderprufe U Value=5.57; Is Heavy Duty Mullion=0 mm  [stored 0 ft]; Limit Sash Width Left Max=891 mm; Limit Sash Width Left Min=300 mm; Max Pane Area=0.81 m²; Sash Height=1733 mm; Sash Width Left=596 mm; Sash Width Right=596 mm; Standard Interlocker=Yes; Width=1190 mm  [stored 3.9042 ft]; Windload Design=1000 mm  [stored 3.28084 ft]
- 1000SW-1518XX-1000Pa: Area Left Sash Glazing=1.05 m²; Area Right Sash Glazing=1.05 m²; Clearvue SHGC Value=0.713; Clearvue U Value=5.75; Custom Windload=1000 mm  [stored 3.28084 ft]; Custom Window Height=1790 mm  [stored 5.8727 ft]; Custom Window Width=1490 mm  [stored 4.88845 ft]; Energy Advantage SHGC Value=0.637; Energy Advantage U Value=4.17; Heavy Duty Interlocker=Yes; Height=1790 mm  [stored 5.8727 ft]; Intruderprufe LowE SHGC Value=0.592; Intruderprufe LowE U Value=4.11; Intruderprufe SHGC Value=0.676; Intruderprufe U Value=5.64; Is Heavy Duty Mullion=1 mm  [stored 0.00328084 ft]; Limit Sash Width Left Max=1191 mm; Limit Sash Width Left Min=300 mm; Max Pane Area=1.05 m²; Sash Height=1733 mm; Sash Width Left=746 mm; Sash Width Right=746 mm; Standard Interlocker=No; Width=1490 mm  [stored 4.88845 ft]; Windload Design=1000 mm  [stored 3.28084 ft]
- 1000SW-1818XX-1000Pa: Area Left Sash Glazing=1.3 m²; Area Right Sash Glazing=1.3 m²; Clearvue SHGC Value=0.723; Clearvue U Value=5.8; Custom Windload=1000 mm  [stored 3.28084 ft]; Custom Window Height=1790 mm  [stored 5.8727 ft]; Custom Window Width=1790 mm  [stored 5.8727 ft]; Energy Advantage SHGC Value=0.646; Energy Advantage U Value=4.15; Heavy Duty Interlocker=Yes; Height=1790 mm  [stored 5.8727 ft]; Intruderprufe LowE SHGC Value=0.6; Intruderprufe LowE U Value=4.09; Intruderprufe SHGC Value=0.686; Intruderprufe U Value=5.68; Is Heavy Duty Mullion=1 mm  [stored 0.00328084 ft]; Limit Sash Width Left Max=1491 mm; Limit Sash Width Left Min=300 mm; Max Pane Area=1.3 m²; Sash Height=1733 mm; Sash Width Left=896 mm; Sash Width Right=896 mm; Standard Interlocker=No; Width=1790 mm  [stored 5.8727 ft]; Windload Design=1000 mm  [stored 3.28084 ft]
- 1000SW-2118XX-1000Pa: Area Left Sash Glazing=1.54 m²; Area Right Sash Glazing=1.54 m²; Clearvue SHGC Value=0.73; Clearvue U Value=5.83; Custom Windload=1000 mm  [stored 3.28084 ft]; Custom Window Height=1790 mm  [stored 5.8727 ft]; Custom Window Width=2090 mm  [stored 6.85696 ft]; Energy Advantage SHGC Value=0.652; Energy Advantage U Value=4.14; Heavy Duty Interlocker=Yes; Height=1790 mm  [stored 5.8727 ft]; Intruderprufe LowE SHGC Value=0.605; Intruderprufe LowE U Value=4.08; Intruderprufe SHGC Value=0.693; Intruderprufe U Value=5.71; Is Heavy Duty Mullion=1 mm  [stored 0.00328084 ft]; Limit Sash Width Left Max=1500 mm  [stored 4.92126 ft]; Limit Sash Width Left Min=591 mm; Max Pane Area=1.54 m²; Sash Height=1733 mm; Sash Width Left=1046 mm; Sash Width Right=1046 mm; Standard Interlocker=No; Width=2090 mm  [stored 6.85696 ft]; Windload Design=1000 mm  [stored 3.28084 ft]
- 1000SW-2418XX-1000Pa: Area Left Sash Glazing=1.79 m²; Area Right Sash Glazing=1.79 m²; Clearvue SHGC Value=0.735; Clearvue U Value=5.86; Custom Windload=1000 mm  [stored 3.28084 ft]; Custom Window Height=1790 mm  [stored 5.8727 ft]; Custom Window Width=2390 mm  [stored 7.84121 ft]; Energy Advantage SHGC Value=0.657; Energy Advantage U Value=4.13; Heavy Duty Interlocker=Yes; Height=1790 mm  [stored 5.8727 ft]; Intruderprufe LowE SHGC Value=0.61; Intruderprufe LowE U Value=4.07; Intruderprufe SHGC Value=0.698; Intruderprufe U Value=5.74; Is Heavy Duty Mullion=1 mm  [stored 0.00328084 ft]; Limit Sash Width Left Max=1500 mm  [stored 4.92126 ft]; Limit Sash Width Left Min=891 mm; Max Pane Area=1.79 m²; Sash Height=1733 mm; Sash Width Left=1196 mm; Sash Width Right=1196 mm; Standard Interlocker=No; Width=2390 mm  [stored 7.84121 ft]; Windload Design=1000 mm  [stored 3.28084 ft]
- 1000SW-2718XX-1000Pa: Area Left Sash Glazing=2.03 m²; Area Right Sash Glazing=2.03 m²; Clearvue SHGC Value=0.74; Clearvue U Value=5.88; Custom Windload=1000 mm  [stored 3.28084 ft]; Custom Window Height=1790 mm  [stored 5.8727 ft]; Custom Window Width=2690 mm; Energy Advantage SHGC Value=0.661; Energy Advantage U Value=4.13; Heavy Duty Interlocker=Yes; Height=1790 mm  [stored 5.8727 ft]; Intruderprufe LowE SHGC Value=0.613; Intruderprufe LowE U Value=4.07; Intruderprufe SHGC Value=0.702; Intruderprufe U Value=5.76; Is Heavy Duty Mullion=1 mm  [stored 0.00328084 ft]; Limit Sash Width Left Max=1500 mm  [stored 4.92126 ft]; Limit Sash Width Left Min=1191 mm; Max Pane Area=2.03 m²; Sash Height=1733 mm; Sash Width Left=1346 mm; Sash Width Right=1346 mm; Standard Interlocker=No; Width=2690 mm; Windload Design=1000 mm  [stored 3.28084 ft]
- 1000SW-3018XX-1000Pa: Area Left Sash Glazing=2.28 m²; Area Right Sash Glazing=2.28 m²; Clearvue SHGC Value=0.743; Clearvue U Value=5.9; Custom Windload=1000 mm  [stored 3.28084 ft]; Custom Window Height=1790 mm  [stored 5.8727 ft]; Custom Window Width=2990 mm  [stored 9.80971 ft]; Energy Advantage SHGC Value=0.664; Energy Advantage U Value=4.12; Heavy Duty Interlocker=Yes; Height=1790 mm  [stored 5.8727 ft]; Intruderprufe LowE SHGC Value=0.616; Intruderprufe LowE U Value=4.06; Intruderprufe SHGC Value=0.705; Intruderprufe U Value=5.77; Is Heavy Duty Mullion=1 mm  [stored 0.00328084 ft]; Limit Sash Width Left Max=1500 mm  [stored 4.92126 ft]; Limit Sash Width Left Min=1491 mm; Max Pane Area=2.28 m²; Sash Height=1733 mm; Sash Width Left=1496 mm; Sash Width Right=1496 mm; Standard Interlocker=No; Width=2990 mm  [stored 9.80971 ft]; Windload Design=1000 mm  [stored 3.28084 ft]
- 1000SW-0906XX-1500Pa: Area Left Sash Glazing=0.15 m²; Area Right Sash Glazing=0.15 m²; Clearvue SHGC Value=0.536; Clearvue U Value=5.91; Custom Windload=1500 mm  [stored 4.92126 ft]; Custom Window Height=590 mm  [stored 1.9357 ft]; Custom Window Width=890 mm  [stored 2.91995 ft]; Energy Advantage SHGC Value=0.481; Energy Advantage U Value=4.85; Heavy Duty Interlocker=No; Height=590 mm  [stored 1.9357 ft]; Intruderprufe LowE SHGC Value=0.444; Intruderprufe LowE U Value=4.814; Intruderprufe SHGC Value=0.509; Intruderprufe U Value=5.8; Is Heavy Duty Mullion=0 mm  [stored 0 ft]; Limit Sash Width Left Max=591 mm; Limit Sash Width Left Min=300 mm; Max Pane Area=0.15 m²; Sash Height=533 mm; Sash Width Left=446 mm; Sash Width Right=446 mm; Standard Interlocker=Yes; Width=890 mm  [stored 2.91995 ft]; Windload Design=1500 mm  [stored 4.92126 ft]
- 1000SW-0906XX-2000Pa: Area Left Sash Glazing=0.15 m²; Area Right Sash Glazing=0.15 m²; Clearvue SHGC Value=0.536; Clearvue U Value=5.91; Custom Windload=2000 mm  [stored 6.56168 ft]; Custom Window Height=590 mm  [stored 1.9357 ft]; Custom Window Width=890 mm  [stored 2.91995 ft]; Energy Advantage SHGC Value=0.481; Energy Advantage U Value=4.85; Heavy Duty Interlocker=No; Height=590 mm  [stored 1.9357 ft]; Intruderprufe LowE SHGC Value=0.444; Intruderprufe LowE U Value=4.814; Intruderprufe SHGC Value=0.509; Intruderprufe U Value=5.8; Is Heavy Duty Mullion=0 mm  [stored 0 ft]; Limit Sash Width Left Max=591 mm; Limit Sash Width Left Min=300 mm; Max Pane Area=0.15 m²; Sash Height=533 mm; Sash Width Left=446 mm; Sash Width Right=446 mm; Standard Interlocker=Yes; Width=890 mm  [stored 2.91995 ft]; Windload Design=2000 mm  [stored 6.56168 ft]
- 1000SW-0909XX-1500Pa: Area Left Sash Glazing=0.25 m²; Area Right Sash Glazing=0.25 m²; Clearvue SHGC Value=0.604; Clearvue U Value=5.73; Custom Windload=1500 mm  [stored 4.92126 ft]; Custom Window Height=890 mm  [stored 2.91995 ft]; Custom Window Width=890 mm  [stored 2.91995 ft]; Energy Advantage SHGC Value=0.541; Energy Advantage U Value=4.54; Heavy Duty Interlocker=No; Height=890 mm  [stored 2.91995 ft]; Intruderprufe LowE SHGC Value=0.502; Intruderprufe LowE U Value=4.49; Intruderprufe SHGC Value=0.574; Intruderprufe U Value=5.63; Is Heavy Duty Mullion=0 mm  [stored 0 ft]; Limit Sash Width Left Max=591 mm; Limit Sash Width Left Min=300 mm; Max Pane Area=0.25 m²; Sash Height=833 mm; Sash Width Left=446 mm; Sash Width Right=446 mm; Standard Interlocker=Yes; Width=890 mm  [stored 2.91995 ft]; Windload Design=1500 mm  [stored 4.92126 ft]
- 1000SW-0909XX-2000Pa: Area Left Sash Glazing=0.25 m²; Area Right Sash Glazing=0.25 m²; Clearvue SHGC Value=0.604; Clearvue U Value=5.73; Custom Windload=2000 mm  [stored 6.56168 ft]; Custom Window Height=890 mm  [stored 2.91995 ft]; Custom Window Width=890 mm  [stored 2.91995 ft]; Energy Advantage SHGC Value=0.541; Energy Advantage U Value=4.54; Heavy Duty Interlocker=No; Height=890 mm  [stored 2.91995 ft]; Intruderprufe LowE SHGC Value=0.502; Intruderprufe LowE U Value=4.49; Intruderprufe SHGC Value=0.574; Intruderprufe U Value=5.63; Is Heavy Duty Mullion=0 mm  [stored 0 ft]; Limit Sash Width Left Max=591 mm; Limit Sash Width Left Min=300 mm; Max Pane Area=0.25 m²; Sash Height=833 mm; Sash Width Left=446 mm; Sash Width Right=446 mm; Standard Interlocker=Yes; Width=890 mm  [stored 2.91995 ft]; Windload Design=2000 mm  [stored 6.56168 ft]
- 1000SW-0912XX-1500Pa: Area Left Sash Glazing=0.36 m²; Area Right Sash Glazing=0.36 m²; Clearvue SHGC Value=2.638; Clearvue U Value=5.65; Custom Windload=1500 mm  [stored 4.92126 ft]; Custom Window Height=1190 mm  [stored 3.9042 ft]; Custom Window Width=890 mm  [stored 2.91995 ft]; Energy Advantage SHGC Value=0.572; Energy Advantage U Value=4.39; Heavy Duty Interlocker=No; Height=1190 mm  [stored 3.9042 ft]; Intruderprufe LowE SHGC Value=0.531; Intruderprufe LowE U Value=4.33; Intruderprufe SHGC Value=0.606; Intruderprufe U Value=5.54; Is Heavy Duty Mullion=0 mm  [stored 0 ft]; Limit Sash Width Left Max=591 mm; Limit Sash Width Left Min=300 mm; Max Pane Area=0.36 m²; Sash Height=1133 mm; Sash Width Left=446 mm; Sash Width Right=446 mm; Standard Interlocker=Yes; Width=890 mm  [stored 2.91995 ft]; Windload Design=1500 mm  [stored 4.92126 ft]
- 1000SW-0912XX-2000Pa: Area Left Sash Glazing=0.36 m²; Area Right Sash Glazing=0.36 m²; Clearvue SHGC Value=2.638; Clearvue U Value=5.65; Custom Windload=2000 mm  [stored 6.56168 ft]; Custom Window Height=1190 mm  [stored 3.9042 ft]; Custom Window Width=890 mm  [stored 2.91995 ft]; Energy Advantage SHGC Value=0.572; Energy Advantage U Value=4.39; Heavy Duty Interlocker=No; Height=1190 mm  [stored 3.9042 ft]; Intruderprufe LowE SHGC Value=0.531; Intruderprufe LowE U Value=4.33; Intruderprufe SHGC Value=0.606; Intruderprufe U Value=5.54; Is Heavy Duty Mullion=0 mm  [stored 0 ft]; Limit Sash Width Left Max=591 mm; Limit Sash Width Left Min=300 mm; Max Pane Area=0.36 m²; Sash Height=1133 mm; Sash Width Left=446 mm; Sash Width Right=446 mm; Standard Interlocker=Yes; Width=890 mm  [stored 2.91995 ft]; Windload Design=2000 mm  [stored 6.56168 ft]
- 1000SW-0915XX-1500Pa: Area Left Sash Glazing=0.46 m²; Area Right Sash Glazing=0.46 m²; Clearvue SHGC Value=0.658; Clearvue U Value=5.6; Custom Windload=1500 mm  [stored 4.92126 ft]; Custom Window Height=1490 mm  [stored 4.88845 ft]; Custom Window Width=890 mm  [stored 2.91995 ft]; Energy Advantage SHGC Value=0.59; Energy Advantage U Value=4.29; Heavy Duty Interlocker=No; Height=1490 mm  [stored 4.88845 ft]; Intruderprufe LowE SHGC Value=0.548; Intruderprufe LowE U Value=4.23; Intruderprufe SHGC Value=0.625; Intruderprufe U Value=5.49; Is Heavy Duty Mullion=0 mm  [stored 0 ft]; Limit Sash Width Left Max=591 mm; Limit Sash Width Left Min=300 mm; Max Pane Area=0.46 m²; Sash Height=1433 mm; Sash Width Left=446 mm; Sash Width Right=446 mm; Standard Interlocker=Yes; Width=890 mm  [stored 2.91995 ft]; Windload Design=1500 mm  [stored 4.92126 ft]
- 1000SW-0915XX-2000Pa: Area Left Sash Glazing=0.46 m²; Area Right Sash Glazing=0.46 m²; Clearvue SHGC Value=0.658; Clearvue U Value=5.6; Custom Windload=2000 mm  [stored 6.56168 ft]; Custom Window Height=1490 mm  [stored 4.88845 ft]; Custom Window Width=890 mm  [stored 2.91995 ft]; Energy Advantage SHGC Value=0.59; Energy Advantage U Value=4.29; Heavy Duty Interlocker=No; Height=1490 mm  [stored 4.88845 ft]; Intruderprufe LowE SHGC Value=0.548; Intruderprufe LowE U Value=4.23; Intruderprufe SHGC Value=0.625; Intruderprufe U Value=5.49; Is Heavy Duty Mullion=0 mm  [stored 0 ft]; Limit Sash Width Left Max=591 mm; Limit Sash Width Left Min=300 mm; Max Pane Area=0.46 m²; Sash Height=1433 mm; Sash Width Left=446 mm; Sash Width Right=446 mm; Standard Interlocker=Yes; Width=890 mm  [stored 2.91995 ft]; Windload Design=2000 mm  [stored 6.56168 ft]
- 1000SW-1206XX-1500Pa: Area Left Sash Glazing=0.21 m²; Area Right Sash Glazing=0.21 m²; Clearvue SHGC Value=0.627; Clearvue U Value=5.85; Custom Windload=1500 mm  [stored 4.92126 ft]; Custom Window Height=590 mm  [stored 1.9357 ft]; Custom Window Width=1190 mm  [stored 3.9042 ft]; Energy Advantage SHGC Value=0.562; Energy Advantage U Value=4.52; Heavy Duty Interlocker=No; Height=590 mm  [stored 1.9357 ft]; Intruderprufe LowE SHGC Value=0.525; Intruderprufe LowE U Value=4.47; Intruderprufe SHGC Value=0.595; Intruderprufe U Value=5.91; Is Heavy Duty Mullion=0 mm  [stored 0 ft]; Limit Sash Width Left Max=891 mm; Limit Sash Width Left Min=300 mm; Max Pane Area=0.21 m²; Sash Height=533 mm; Sash Width Left=596 mm; Sash Width Right=596 mm; Standard Interlocker=Yes; Width=1190 mm  [stored 3.9042 ft]; Windload Design=1500 mm  [stored 4.92126 ft]
- 1000SW-1206XX-2000Pa: Area Left Sash Glazing=0.21 m²; Area Right Sash Glazing=0.21 m²; Clearvue SHGC Value=0.627; Clearvue U Value=5.85; Custom Windload=2000 mm  [stored 6.56168 ft]; Custom Window Height=590 mm  [stored 1.9357 ft]; Custom Window Width=1190 mm  [stored 3.9042 ft]; Energy Advantage SHGC Value=0.562; Energy Advantage U Value=4.52; Heavy Duty Interlocker=No; Height=590 mm  [stored 1.9357 ft]; Intruderprufe LowE SHGC Value=0.525; Intruderprufe LowE U Value=4.47; Intruderprufe SHGC Value=0.595; Intruderprufe U Value=5.91; Is Heavy Duty Mullion=0 mm  [stored 0 ft]; Limit Sash Width Left Max=891 mm; Limit Sash Width Left Min=300 mm; Max Pane Area=0.21 m²; Sash Height=533 mm; Sash Width Left=596 mm; Sash Width Right=596 mm; Standard Interlocker=Yes; Width=1190 mm  [stored 3.9042 ft]; Windload Design=2000 mm  [stored 6.56168 ft]
- 1000SW-1209XX-1500Pa: Area Left Sash Glazing=0.36 m²; Area Right Sash Glazing=0.36 m²; Clearvue SHGC Value=0.627; Clearvue U Value=5.85; Custom Windload=1500 mm  [stored 4.92126 ft]; Custom Window Height=890 mm  [stored 2.91995 ft]; Custom Window Width=1190 mm  [stored 3.9042 ft]; Energy Advantage SHGC Value=0.562; Energy Advantage U Value=4.52; Heavy Duty Interlocker=No; Height=890 mm  [stored 2.91995 ft]; Intruderprufe LowE SHGC Value=0.52; Intruderprufe LowE U Value=4.47; Intruderprufe SHGC Value=0.595; Intruderprufe U Value=5.74; Is Heavy Duty Mullion=0 mm  [stored 0 ft]; Limit Sash Width Left Max=891 mm; Limit Sash Width Left Min=300 mm; Max Pane Area=0.36 m²; Sash Height=833 mm; Sash Width Left=596 mm; Sash Width Right=596 mm; Standard Interlocker=Yes; Width=1190 mm  [stored 3.9042 ft]; Windload Design=1500 mm  [stored 4.92126 ft]
- 1000SW-1209XX-2000Pa: Area Left Sash Glazing=0.36 m²; Area Right Sash Glazing=0.36 m²; Clearvue SHGC Value=0.627; Clearvue U Value=5.85; Custom Windload=2000 mm  [stored 6.56168 ft]; Custom Window Height=890 mm  [stored 2.91995 ft]; Custom Window Width=1190 mm  [stored 3.9042 ft]; Energy Advantage SHGC Value=0.562; Energy Advantage U Value=4.52; Heavy Duty Interlocker=No; Height=890 mm  [stored 2.91995 ft]; Intruderprufe LowE SHGC Value=0.52; Intruderprufe LowE U Value=4.47; Intruderprufe SHGC Value=0.595; Intruderprufe U Value=5.74; Is Heavy Duty Mullion=0 mm  [stored 0 ft]; Limit Sash Width Left Max=891 mm; Limit Sash Width Left Min=300 mm; Max Pane Area=0.36 m²; Sash Height=833 mm; Sash Width Left=596 mm; Sash Width Right=596 mm; Standard Interlocker=Yes; Width=1190 mm  [stored 3.9042 ft]; Windload Design=2000 mm  [stored 6.56168 ft]
- 1000SW-1212XX-1500Pa: Area Left Sash Glazing=0.51 m²; Area Right Sash Glazing=0.51 m²; Clearvue SHGC Value=0.662; Clearvue U Value=5.77; Custom Windload=1500 mm  [stored 4.92126 ft]; Custom Window Height=1190 mm  [stored 3.9042 ft]; Custom Window Width=1190 mm  [stored 3.9042 ft]; Energy Advantage SHGC Value=0.593; Energy Advantage U Value=4.35; Heavy Duty Interlocker=No; Height=1190 mm  [stored 3.9042 ft]; Intruderprufe LowE SHGC Value=0.55; Intruderprufe LowE U Value=4.3; Intruderprufe SHGC Value=0.629; Intruderprufe U Value=5.65; Is Heavy Duty Mullion=0 mm  [stored 0 ft]; Limit Sash Width Left Max=891 mm; Limit Sash Width Left Min=300 mm; Max Pane Area=0.51 m²; Sash Height=1133 mm; Sash Width Left=596 mm; Sash Width Right=596 mm; Standard Interlocker=Yes; Width=1190 mm  [stored 3.9042 ft]; Windload Design=1500 mm  [stored 4.92126 ft]
- 1000SW-1212XX-2000Pa: Area Left Sash Glazing=0.51 m²; Area Right Sash Glazing=0.51 m²; Clearvue SHGC Value=0.662; Clearvue U Value=5.77; Custom Windload=2000 mm  [stored 6.56168 ft]; Custom Window Height=1190 mm  [stored 3.9042 ft]; Custom Window Width=1190 mm  [stored 3.9042 ft]; Energy Advantage SHGC Value=0.593; Energy Advantage U Value=4.35; Heavy Duty Interlocker=No; Height=1190 mm  [stored 3.9042 ft]; Intruderprufe LowE SHGC Value=0.55; Intruderprufe LowE U Value=4.3; Intruderprufe SHGC Value=0.629; Intruderprufe U Value=5.65; Is Heavy Duty Mullion=0 mm  [stored 0 ft]; Limit Sash Width Left Max=891 mm; Limit Sash Width Left Min=300 mm; Max Pane Area=0.51 m²; Sash Height=1133 mm; Sash Width Left=596 mm; Sash Width Right=596 mm; Standard Interlocker=Yes; Width=1190 mm  [stored 3.9042 ft]; Windload Design=2000 mm  [stored 6.56168 ft]
- 1000SW-1215XX-1500Pa: Area Left Sash Glazing=0.66 m²; Area Right Sash Glazing=0.66 m²; Clearvue SHGC Value=0.683; Clearvue U Value=5.72; Custom Windload=1500 mm  [stored 4.92126 ft]; Custom Window Height=1490 mm  [stored 4.88845 ft]; Custom Window Width=1190 mm  [stored 3.9042 ft]; Energy Advantage SHGC Value=0.611; Energy Advantage U Value=4.26; Heavy Duty Interlocker=No; Height=1490 mm  [stored 4.88845 ft]; Intruderprufe LowE SHGC Value=0.568; Intruderprufe LowE U Value=4.2; Intruderprufe SHGC Value=0.649; Intruderprufe U Value=5.6; Is Heavy Duty Mullion=0 mm  [stored 0 ft]; Limit Sash Width Left Max=891 mm; Limit Sash Width Left Min=300 mm; Max Pane Area=0.66 m²; Sash Height=1433 mm; Sash Width Left=596 mm; Sash Width Right=596 mm; Standard Interlocker=Yes; Width=1190 mm  [stored 3.9042 ft]; Windload Design=1500 mm  [stored 4.92126 ft]
- 1000SW-1215XX-2000Pa: Area Left Sash Glazing=0.66 m²; Area Right Sash Glazing=0.66 m²; Clearvue SHGC Value=0.683; Clearvue U Value=5.72; Custom Windload=2000 mm  [stored 6.56168 ft]; Custom Window Height=1490 mm  [stored 4.88845 ft]; Custom Window Width=1190 mm  [stored 3.9042 ft]; Energy Advantage SHGC Value=0.611; Energy Advantage U Value=4.26; Heavy Duty Interlocker=No; Height=1490 mm  [stored 4.88845 ft]; Intruderprufe LowE SHGC Value=0.568; Intruderprufe LowE U Value=4.2; Intruderprufe SHGC Value=0.649; Intruderprufe U Value=5.6; Is Heavy Duty Mullion=0 mm  [stored 0 ft]; Limit Sash Width Left Max=891 mm; Limit Sash Width Left Min=300 mm; Max Pane Area=0.66 m²; Sash Height=1433 mm; Sash Width Left=596 mm; Sash Width Right=596 mm; Standard Interlocker=Yes; Width=1190 mm  [stored 3.9042 ft]; Windload Design=2000 mm  [stored 6.56168 ft]
- 1000SW-1218XX-1500Pa: Area Left Sash Glazing=0.81 m²; Area Right Sash Glazing=0.81 m²; Clearvue SHGC Value=0.697; Clearvue U Value=5.68; Custom Windload=1500 mm  [stored 4.92126 ft]; Custom Window Height=1790 mm  [stored 5.8727 ft]; Custom Window Width=1190 mm  [stored 3.9042 ft]; Energy Advantage SHGC Value=0.624; Energy Advantage U Value=4.19; Heavy Duty Interlocker=Yes; Height=1790 mm  [stored 5.8727 ft]; Intruderprufe LowE SHGC Value=0.579; Intruderprufe LowE U Value=4.13; Intruderprufe SHGC Value=0.662; Intruderprufe U Value=5.57; Is Heavy Duty Mullion=1 mm  [stored 0.00328084 ft]; Limit Sash Width Left Max=891 mm; Limit Sash Width Left Min=300 mm; Max Pane Area=0.81 m²; Sash Height=1733 mm; Sash Width Left=596 mm; Sash Width Right=596 mm; Standard Interlocker=No; Width=1190 mm  [stored 3.9042 ft]; Windload Design=1500 mm  [stored 4.92126 ft]
- 1000SW-1218XX-2000Pa: Area Left Sash Glazing=0.81 m²; Area Right Sash Glazing=0.81 m²; Clearvue SHGC Value=0.697; Clearvue U Value=5.68; Custom Windload=2000 mm  [stored 6.56168 ft]; Custom Window Height=1790 mm  [stored 5.8727 ft]; Custom Window Width=1190 mm  [stored 3.9042 ft]; Energy Advantage SHGC Value=0.624; Energy Advantage U Value=4.19; Heavy Duty Interlocker=Yes; Height=1790 mm  [stored 5.8727 ft]; Intruderprufe LowE SHGC Value=0.579; Intruderprufe LowE U Value=4.13; Intruderprufe SHGC Value=0.662; Intruderprufe U Value=5.57; Is Heavy Duty Mullion=1 mm  [stored 0.00328084 ft]; Limit Sash Width Left Max=891 mm; Limit Sash Width Left Min=300 mm; Max Pane Area=0.81 m²; Sash Height=1733 mm; Sash Width Left=596 mm; Sash Width Right=596 mm; Standard Interlocker=No; Width=1190 mm  [stored 3.9042 ft]; Windload Design=2000 mm  [stored 6.56168 ft]
- 1000SW-1506XX-1500Pa: Area Left Sash Glazing=0.28 m²; Area Right Sash Glazing=0.28 m²; Clearvue SHGC Value=0.568; Clearvue U Value=6.09; Custom Windload=1500 mm  [stored 4.92126 ft]; Custom Window Height=590 mm  [stored 1.9357 ft]; Custom Window Width=1490 mm  [stored 4.88845 ft]; Energy Advantage SHGC Value=0.509; Energy Advantage U Value=4.84; Heavy Duty Interlocker=No; Height=590 mm  [stored 1.9357 ft]; Intruderprufe LowE SHGC Value=0.459; Intruderprufe LowE U Value=4.81; Intruderprufe SHGC Value=0.539; Intruderprufe U Value=5.98; Is Heavy Duty Mullion=0 mm  [stored 0 ft]; Limit Sash Width Left Max=1191 mm; Limit Sash Width Left Min=300 mm; Max Pane Area=0.28 m²; Sash Height=533 mm; Sash Width Left=746 mm; Sash Width Right=746 mm; Standard Interlocker=Yes; Width=1490 mm  [stored 4.88845 ft]; Windload Design=1500 mm  [stored 4.92126 ft]
- 1000SW-1506XX-2000Pa: Area Left Sash Glazing=0.28 m²; Area Right Sash Glazing=0.28 m²; Clearvue SHGC Value=0.568; Clearvue U Value=6.09; Custom Windload=2000 mm  [stored 6.56168 ft]; Custom Window Height=590 mm  [stored 1.9357 ft]; Custom Window Width=1490 mm  [stored 4.88845 ft]; Energy Advantage SHGC Value=0.509; Energy Advantage U Value=4.84; Heavy Duty Interlocker=No; Height=590 mm  [stored 1.9357 ft]; Intruderprufe LowE SHGC Value=0.459; Intruderprufe LowE U Value=4.81; Intruderprufe SHGC Value=0.539; Intruderprufe U Value=5.98; Is Heavy Duty Mullion=0 mm  [stored 0 ft]; Limit Sash Width Left Max=1191 mm; Limit Sash Width Left Min=300 mm; Max Pane Area=0.28 m²; Sash Height=533 mm; Sash Width Left=746 mm; Sash Width Right=746 mm; Standard Interlocker=Yes; Width=1490 mm  [stored 4.88845 ft]; Windload Design=2000 mm  [stored 6.56168 ft]
- 1000SW-1509XX-1500Pa: Area Left Sash Glazing=0.47 m²; Area Right Sash Glazing=0.47 m²; Clearvue SHGC Value=0.641; Clearvue U Value=5.92; Custom Windload=1500 mm  [stored 4.92126 ft]; Custom Window Height=890 mm  [stored 2.91995 ft]; Custom Window Width=1490 mm  [stored 4.88845 ft]; Energy Advantage SHGC Value=0.573; Energy Advantage U Value=4.5; Heavy Duty Interlocker=No; Height=890 mm  [stored 2.91995 ft]; Intruderprufe LowE SHGC Value=0.531; Intruderprufe LowE U Value=4.45; Intruderprufe SHGC Value=0.608; Intruderprufe U Value=5.81; Is Heavy Duty Mullion=0 mm  [stored 0 ft]; Limit Sash Width Left Max=1191 mm; Limit Sash Width Left Min=300 mm; Max Pane Area=0.47 m²; Sash Height=833 mm; Sash Width Left=746 mm; Sash Width Right=746 mm; Standard Interlocker=Yes; Width=1490 mm  [stored 4.88845 ft]; Windload Design=1500 mm  [stored 4.92126 ft]
- 1000SW-1509XX-2000Pa: Area Left Sash Glazing=0.47 m²; Area Right Sash Glazing=0.47 m²; Clearvue SHGC Value=0.641; Clearvue U Value=5.92; Custom Windload=2000 mm  [stored 6.56168 ft]; Custom Window Height=890 mm  [stored 2.91995 ft]; Custom Window Width=1490 mm  [stored 4.88845 ft]; Energy Advantage SHGC Value=0.573; Energy Advantage U Value=4.5; Heavy Duty Interlocker=No; Height=890 mm  [stored 2.91995 ft]; Intruderprufe LowE SHGC Value=0.531; Intruderprufe LowE U Value=4.45; Intruderprufe SHGC Value=0.608; Intruderprufe U Value=5.81; Is Heavy Duty Mullion=0 mm  [stored 0 ft]; Limit Sash Width Left Max=1191 mm; Limit Sash Width Left Min=300 mm; Max Pane Area=0.47 m²; Sash Height=833 mm; Sash Width Left=746 mm; Sash Width Right=746 mm; Standard Interlocker=Yes; Width=1490 mm  [stored 4.88845 ft]; Windload Design=2000 mm  [stored 6.56168 ft]
- 1000SW-1512XX-1500Pa: Area Left Sash Glazing=0.67 m²; Area Right Sash Glazing=0.67 m²; Clearvue SHGC Value=0.677; Clearvue U Value=5.84; Custom Windload=1500 mm  [stored 4.92126 ft]; Custom Window Height=1190 mm  [stored 3.9042 ft]; Custom Window Width=1490 mm  [stored 4.88845 ft]; Energy Advantage SHGC Value=0.605; Energy Advantage U Value=4.34; Heavy Duty Interlocker=No; Height=1190 mm  [stored 3.9042 ft]; Intruderprufe LowE SHGC Value=0.561; Intruderprufe LowE U Value=4.28; Intruderprufe SHGC Value=0.642; Intruderprufe U Value=5.72; Is Heavy Duty Mullion=0 mm  [stored 0 ft]; Limit Sash Width Left Max=1191 mm; Limit Sash Width Left Min=300 mm; Max Pane Area=0.67 m²; Sash Height=1133 mm; Sash Width Left=746 mm; Sash Width Right=746 mm; Standard Interlocker=Yes; Width=1490 mm  [stored 4.88845 ft]; Windload Design=1500 mm  [stored 4.92126 ft]
- 1000SW-1512XX-2000Pa: Area Left Sash Glazing=0.67 m²; Area Right Sash Glazing=0.67 m²; Clearvue SHGC Value=0.677; Clearvue U Value=5.84; Custom Windload=2000 mm  [stored 6.56168 ft]; Custom Window Height=1190 mm  [stored 3.9042 ft]; Custom Window Width=1490 mm  [stored 4.88845 ft]; Energy Advantage SHGC Value=0.605; Energy Advantage U Value=4.34; Heavy Duty Interlocker=No; Height=1190 mm  [stored 3.9042 ft]; Intruderprufe LowE SHGC Value=0.561; Intruderprufe LowE U Value=4.28; Intruderprufe SHGC Value=0.642; Intruderprufe U Value=5.72; Is Heavy Duty Mullion=0 mm  [stored 0 ft]; Limit Sash Width Left Max=1191 mm; Limit Sash Width Left Min=300 mm; Max Pane Area=0.67 m²; Sash Height=1133 mm; Sash Width Left=746 mm; Sash Width Right=746 mm; Standard Interlocker=Yes; Width=1490 mm  [stored 4.88845 ft]; Windload Design=2000 mm  [stored 6.56168 ft]
- 1000SW-1515XX-1500Pa: Area Left Sash Glazing=0.86 m²; Area Right Sash Glazing=0.86 m²; Clearvue SHGC Value=0.698; Clearvue U Value=5.79; Custom Windload=1500 mm  [stored 4.92126 ft]; Custom Window Height=1490 mm  [stored 4.88845 ft]; Custom Window Width=1490 mm  [stored 4.88845 ft]; Energy Advantage SHGC Value=0.625; Energy Advantage U Value=4.24; Heavy Duty Interlocker=No; Height=1490 mm  [stored 4.88845 ft]; Intruderprufe LowE SHGC Value=0.58; Intruderprufe LowE U Value=4.18; Intruderprufe SHGC Value=0.663; Intruderprufe U Value=5.67; Is Heavy Duty Mullion=0 mm  [stored 0 ft]; Limit Sash Width Left Max=1191 mm; Limit Sash Width Left Min=300 mm; Max Pane Area=0.86 m²; Sash Height=1433 mm; Sash Width Left=746 mm; Sash Width Right=746 mm; Standard Interlocker=Yes; Width=1490 mm  [stored 4.88845 ft]; Windload Design=1500 mm  [stored 4.92126 ft]
- 1000SW-1515XX-2000Pa: Area Left Sash Glazing=0.86 m²; Area Right Sash Glazing=0.86 m²; Clearvue SHGC Value=0.698; Clearvue U Value=5.79; Custom Windload=2000 mm  [stored 6.56168 ft]; Custom Window Height=1490 mm  [stored 4.88845 ft]; Custom Window Width=1490 mm  [stored 4.88845 ft]; Energy Advantage SHGC Value=0.625; Energy Advantage U Value=4.24; Heavy Duty Interlocker=Yes; Height=1490 mm  [stored 4.88845 ft]; Intruderprufe LowE SHGC Value=0.58; Intruderprufe LowE U Value=4.18; Intruderprufe SHGC Value=0.663; Intruderprufe U Value=5.67; Is Heavy Duty Mullion=1 mm  [stored 0.00328084 ft]; Limit Sash Width Left Max=1191 mm; Limit Sash Width Left Min=300 mm; Max Pane Area=0.86 m²; Sash Height=1433 mm; Sash Width Left=746 mm; Sash Width Right=746 mm; Standard Interlocker=No; Width=1490 mm  [stored 4.88845 ft]; Windload Design=2000 mm  [stored 6.56168 ft]
- 1000SW-1518XX-1500Pa: Area Left Sash Glazing=1.05 m²; Area Right Sash Glazing=1.05 m²; Clearvue SHGC Value=0.713; Clearvue U Value=5.75; Custom Windload=1500 mm  [stored 4.92126 ft]; Custom Window Height=1790 mm  [stored 5.8727 ft]; Custom Window Width=1490 mm  [stored 4.88845 ft]; Energy Advantage SHGC Value=0.637; Energy Advantage U Value=4.17; Heavy Duty Interlocker=Yes; Height=1790 mm  [stored 5.8727 ft]; Intruderprufe LowE SHGC Value=0.592; Intruderprufe LowE U Value=4.11; Intruderprufe SHGC Value=0.676; Intruderprufe U Value=5.64; Is Heavy Duty Mullion=1 mm  [stored 0.00328084 ft]; Limit Sash Width Left Max=1191 mm; Limit Sash Width Left Min=300 mm; Max Pane Area=1.05 m²; Sash Height=1733 mm; Sash Width Left=746 mm; Sash Width Right=746 mm; Standard Interlocker=No; Width=1490 mm  [stored 4.88845 ft]; Windload Design=1500 mm  [stored 4.92126 ft]
- 1000SW-1518XX-2000Pa: Area Left Sash Glazing=1.05 m²; Area Right Sash Glazing=1.05 m²; Clearvue SHGC Value=0.713; Clearvue U Value=5.75; Custom Windload=2000 mm  [stored 6.56168 ft]; Custom Window Height=1790 mm  [stored 5.8727 ft]; Custom Window Width=1490 mm  [stored 4.88845 ft]; Energy Advantage SHGC Value=0.637; Energy Advantage U Value=4.17; Heavy Duty Interlocker=Yes; Height=1790 mm  [stored 5.8727 ft]; Intruderprufe LowE SHGC Value=0.592; Intruderprufe LowE U Value=4.11; Intruderprufe SHGC Value=0.676; Intruderprufe U Value=5.64; Is Heavy Duty Mullion=1 mm  [stored 0.00328084 ft]; Limit Sash Width Left Max=1191 mm; Limit Sash Width Left Min=300 mm; Max Pane Area=1.05 m²; Sash Height=1733 mm; Sash Width Left=746 mm; Sash Width Right=746 mm; Standard Interlocker=No; Width=1490 mm  [stored 4.88845 ft]; Windload Design=2000 mm  [stored 6.56168 ft]
- 1000SW-1806XX-1500Pa: Area Left Sash Glazing=0.34 m²; Area Right Sash Glazing=0.34 m²; Clearvue SHGC Value=0.576; Clearvue U Value=6.14; Custom Windload=1500 mm  [stored 4.92126 ft]; Custom Window Height=590 mm  [stored 1.9357 ft]; Custom Window Width=1790 mm  [stored 5.8727 ft]; Energy Advantage SHGC Value=0.516; Energy Advantage U Value=4.84; Heavy Duty Interlocker=No; Height=590 mm  [stored 1.9357 ft]; Intruderprufe LowE SHGC Value=0.476; Intruderprufe LowE U Value=4.81; Intruderprufe SHGC Value=0.547; Intruderprufe U Value=6.02; Is Heavy Duty Mullion=0 mm  [stored 0 ft]; Limit Sash Width Left Max=1491 mm; Limit Sash Width Left Min=300 mm; Max Pane Area=0.34 m²; Sash Height=533 mm; Sash Width Left=896 mm; Sash Width Right=896 mm; Standard Interlocker=Yes; Width=1790 mm  [stored 5.8727 ft]; Windload Design=1500 mm  [stored 4.92126 ft]
- 1000SW-1806XX-2000Pa: Area Left Sash Glazing=0.34 m²; Area Right Sash Glazing=0.34 m²; Clearvue SHGC Value=0.576; Clearvue U Value=6.14; Custom Windload=2000 mm  [stored 6.56168 ft]; Custom Window Height=590 mm  [stored 1.9357 ft]; Custom Window Width=1790 mm  [stored 5.8727 ft]; Energy Advantage SHGC Value=0.516; Energy Advantage U Value=4.84; Heavy Duty Interlocker=No; Height=590 mm  [stored 1.9357 ft]; Intruderprufe LowE SHGC Value=0.476; Intruderprufe LowE U Value=4.81; Intruderprufe SHGC Value=0.547; Intruderprufe U Value=6.02; Is Heavy Duty Mullion=0 mm  [stored 0 ft]; Limit Sash Width Left Max=1491 mm; Limit Sash Width Left Min=300 mm; Max Pane Area=0.34 m²; Sash Height=533 mm; Sash Width Left=896 mm; Sash Width Right=896 mm; Standard Interlocker=Yes; Width=1790 mm  [stored 5.8727 ft]; Windload Design=2000 mm  [stored 6.56168 ft]
- 1000SW-1809XX-1500Pa: Area Left Sash Glazing=0.58 m²; Area Right Sash Glazing=0.58 m²; Clearvue SHGC Value=0.65; Clearvue U Value=5.97; Custom Windload=1500 mm  [stored 4.92126 ft]; Custom Window Height=890 mm  [stored 2.91995 ft]; Custom Window Width=1790 mm  [stored 5.8727 ft]; Energy Advantage SHGC Value=0.581; Energy Advantage U Value=4.5; Heavy Duty Interlocker=No; Height=890 mm  [stored 2.91995 ft]; Intruderprufe LowE SHGC Value=0.538; Intruderprufe LowE U Value=4.45; Intruderprufe SHGC Value=0.617; Intruderprufe U Value=5.85; Is Heavy Duty Mullion=0 mm  [stored 0 ft]; Limit Sash Width Left Max=1491 mm; Limit Sash Width Left Min=300 mm; Max Pane Area=0.58 m²; Sash Height=833 mm; Sash Width Left=896 mm; Sash Width Right=896 mm; Standard Interlocker=Yes; Width=1790 mm  [stored 5.8727 ft]; Windload Design=1500 mm  [stored 4.92126 ft]
- 1000SW-1809XX-2000Pa: Area Left Sash Glazing=0.58 m²; Area Right Sash Glazing=0.58 m²; Clearvue SHGC Value=0.65; Clearvue U Value=5.97; Custom Windload=2000 mm  [stored 6.56168 ft]; Custom Window Height=890 mm  [stored 2.91995 ft]; Custom Window Width=1790 mm  [stored 5.8727 ft]; Energy Advantage SHGC Value=0.581; Energy Advantage U Value=4.5; Heavy Duty Interlocker=No; Height=890 mm  [stored 2.91995 ft]; Intruderprufe LowE SHGC Value=0.538; Intruderprufe LowE U Value=4.45; Intruderprufe SHGC Value=0.617; Intruderprufe U Value=5.85; Is Heavy Duty Mullion=0 mm  [stored 0 ft]; Limit Sash Width Left Max=1491 mm; Limit Sash Width Left Min=300 mm; Max Pane Area=0.58 m²; Sash Height=833 mm; Sash Width Left=896 mm; Sash Width Right=896 mm; Standard Interlocker=Yes; Width=1790 mm  [stored 5.8727 ft]; Windload Design=2000 mm  [stored 6.56168 ft]
- 1000SW-1812XX-1500Pa: Area Left Sash Glazing=0.82 m²; Area Right Sash Glazing=0.82 m²; Clearvue SHGC Value=0.686; Clearvue U Value=5.88; Custom Windload=1500 mm  [stored 4.92126 ft]; Custom Window Height=1190 mm  [stored 3.9042 ft]; Custom Window Width=1790 mm  [stored 5.8727 ft]; Energy Advantage SHGC Value=0.614; Energy Advantage U Value=4.32; Heavy Duty Interlocker=No; Height=1190 mm  [stored 3.9042 ft]; Intruderprufe LowE SHGC Value=0.569; Intruderprufe LowE U Value=4.27; Intruderprufe SHGC Value=0.651; Intruderprufe U Value=5.77; Is Heavy Duty Mullion=0 mm  [stored 0 ft]; Limit Sash Width Left Max=1491 mm; Limit Sash Width Left Min=300 mm; Max Pane Area=0.82 m²; Sash Height=1133 mm; Sash Width Left=896 mm; Sash Width Right=896 mm; Standard Interlocker=Yes; Width=1790 mm  [stored 5.8727 ft]; Windload Design=1500 mm  [stored 4.92126 ft]
- 1000SW-1812XX-2000Pa: Area Left Sash Glazing=0.82 m²; Area Right Sash Glazing=0.82 m²; Clearvue SHGC Value=0.686; Clearvue U Value=5.88; Custom Windload=2000 mm  [stored 6.56168 ft]; Custom Window Height=1190 mm  [stored 3.9042 ft]; Custom Window Width=1790 mm  [stored 5.8727 ft]; Energy Advantage SHGC Value=0.614; Energy Advantage U Value=4.32; Heavy Duty Interlocker=No; Height=1190 mm  [stored 3.9042 ft]; Intruderprufe LowE SHGC Value=0.569; Intruderprufe LowE U Value=4.27; Intruderprufe SHGC Value=0.651; Intruderprufe U Value=5.77; Is Heavy Duty Mullion=0 mm  [stored 0 ft]; Limit Sash Width Left Max=1491 mm; Limit Sash Width Left Min=300 mm; Max Pane Area=0.82 m²; Sash Height=1133 mm; Sash Width Left=896 mm; Sash Width Right=896 mm; Standard Interlocker=Yes; Width=1790 mm  [stored 5.8727 ft]; Windload Design=2000 mm  [stored 6.56168 ft]
- 1000SW-1815XX-1500Pa: Area Left Sash Glazing=1.06 m²; Area Right Sash Glazing=1.06 m²; Clearvue SHGC Value=0.708; Clearvue U Value=5.83; Custom Windload=1500 mm  [stored 4.92126 ft]; Custom Window Height=1490 mm  [stored 4.88845 ft]; Custom Window Width=1790 mm  [stored 5.8727 ft]; Energy Advantage SHGC Value=0.633; Energy Advantage U Value=4.22; Heavy Duty Interlocker=Yes; Height=1490 mm  [stored 4.88845 ft]; Intruderprufe LowE SHGC Value=0.587; Intruderprufe LowE U Value=4.16; Intruderprufe SHGC Value=0.672; Intruderprufe U Value=5.72; Is Heavy Duty Mullion=1 mm  [stored 0.00328084 ft]; Limit Sash Width Left Max=1491 mm; Limit Sash Width Left Min=300 mm; Max Pane Area=1.06 m²; Sash Height=1433 mm; Sash Width Left=896 mm; Sash Width Right=896 mm; Standard Interlocker=No; Width=1790 mm  [stored 5.8727 ft]; Windload Design=1500 mm  [stored 4.92126 ft]
- 1000SW-1815XX-2000Pa: Area Left Sash Glazing=1.06 m²; Area Right Sash Glazing=1.06 m²; Clearvue SHGC Value=0.708; Clearvue U Value=5.83; Custom Windload=2000 mm  [stored 6.56168 ft]; Custom Window Height=1490 mm  [stored 4.88845 ft]; Custom Window Width=1790 mm  [stored 5.8727 ft]; Energy Advantage SHGC Value=0.633; Energy Advantage U Value=4.22; Heavy Duty Interlocker=Yes; Height=1490 mm  [stored 4.88845 ft]; Intruderprufe LowE SHGC Value=0.587; Intruderprufe LowE U Value=4.16; Intruderprufe SHGC Value=0.672; Intruderprufe U Value=5.72; Is Heavy Duty Mullion=1 mm  [stored 0.00328084 ft]; Limit Sash Width Left Max=1491 mm; Limit Sash Width Left Min=300 mm; Max Pane Area=1.06 m²; Sash Height=1433 mm; Sash Width Left=896 mm; Sash Width Right=896 mm; Standard Interlocker=No; Width=1790 mm  [stored 5.8727 ft]; Windload Design=2000 mm  [stored 6.56168 ft]
- 1000SW-1818XX-1500Pa: Area Left Sash Glazing=1.3 m²; Area Right Sash Glazing=1.3 m²; Clearvue SHGC Value=0.723; Clearvue U Value=5.8; Custom Windload=1500 mm  [stored 4.92126 ft]; Custom Window Height=1790 mm  [stored 5.8727 ft]; Custom Window Width=1790 mm  [stored 5.8727 ft]; Energy Advantage SHGC Value=0.646; Energy Advantage U Value=4.15; Heavy Duty Interlocker=Yes; Height=1790 mm  [stored 5.8727 ft]; Intruderprufe LowE SHGC Value=0.6; Intruderprufe LowE U Value=4.09; Intruderprufe SHGC Value=0.686; Intruderprufe U Value=5.68; Is Heavy Duty Mullion=1 mm  [stored 0.00328084 ft]; Limit Sash Width Left Max=1491 mm; Limit Sash Width Left Min=300 mm; Max Pane Area=1.3 m²; Sash Height=1733 mm; Sash Width Left=896 mm; Sash Width Right=896 mm; Standard Interlocker=No; Width=1790 mm  [stored 5.8727 ft]; Windload Design=1500 mm  [stored 4.92126 ft]
- 1000SW-1818XX-2000Pa: Area Left Sash Glazing=1.3 m²; Area Right Sash Glazing=1.3 m²; Clearvue SHGC Value=0.723; Clearvue U Value=5.8; Custom Windload=2000 mm  [stored 6.56168 ft]; Custom Window Height=1790 mm  [stored 5.8727 ft]; Custom Window Width=1790 mm  [stored 5.8727 ft]; Energy Advantage SHGC Value=0.646; Energy Advantage U Value=4.15; Heavy Duty Interlocker=Yes; Height=1790 mm  [stored 5.8727 ft]; Intruderprufe LowE SHGC Value=0.6; Intruderprufe LowE U Value=4.09; Intruderprufe SHGC Value=0.686; Intruderprufe U Value=5.68; Is Heavy Duty Mullion=1 mm  [stored 0.00328084 ft]; Limit Sash Width Left Max=1491 mm; Limit Sash Width Left Min=300 mm; Max Pane Area=1.3 m²; Sash Height=1733 mm; Sash Width Left=896 mm; Sash Width Right=896 mm; Standard Interlocker=No; Width=1790 mm  [stored 5.8727 ft]; Windload Design=2000 mm  [stored 6.56168 ft]
- 1000SW-2106XX-1500Pa: Area Left Sash Glazing=0.41 m²; Area Right Sash Glazing=0.41 m²; Clearvue SHGC Value=0.581; Clearvue U Value=6.17; Custom Windload=1500 mm  [stored 4.92126 ft]; Custom Window Height=590 mm  [stored 1.9357 ft]; Custom Window Width=2090 mm  [stored 6.85696 ft]; Energy Advantage SHGC Value=0.521; Energy Advantage U Value=4.84; Heavy Duty Interlocker=No; Height=590 mm  [stored 1.9357 ft]; Intruderprufe LowE SHGC Value=0.48; Intruderprufe LowE U Value=4.8; Intruderprufe SHGC Value=0.552; Intruderprufe U Value=6.05; Is Heavy Duty Mullion=0 mm  [stored 0 ft]; Limit Sash Width Left Max=1500 mm  [stored 4.92126 ft]; Limit Sash Width Left Min=591 mm; Max Pane Area=0.41 m²; Sash Height=533 mm; Sash Width Left=1046 mm; Sash Width Right=1046 mm; Standard Interlocker=Yes; Width=2090 mm  [stored 6.85696 ft]; Windload Design=1500 mm  [stored 4.92126 ft]
- 1000SW-2106XX-2000Pa: Area Left Sash Glazing=0.41 m²; Area Right Sash Glazing=0.41 m²; Clearvue SHGC Value=0.581; Clearvue U Value=6.17; Custom Windload=2000 mm  [stored 6.56168 ft]; Custom Window Height=590 mm  [stored 1.9357 ft]; Custom Window Width=2090 mm  [stored 6.85696 ft]; Energy Advantage SHGC Value=0.521; Energy Advantage U Value=4.84; Heavy Duty Interlocker=No; Height=590 mm  [stored 1.9357 ft]; Intruderprufe LowE SHGC Value=0.48; Intruderprufe LowE U Value=4.8; Intruderprufe SHGC Value=0.552; Intruderprufe U Value=6.05; Is Heavy Duty Mullion=0 mm  [stored 0 ft]; Limit Sash Width Left Max=1500 mm  [stored 4.92126 ft]; Limit Sash Width Left Min=591 mm; Max Pane Area=0.41 m²; Sash Height=533 mm; Sash Width Left=1046 mm; Sash Width Right=1046 mm; Standard Interlocker=Yes; Width=2090 mm  [stored 6.85696 ft]; Windload Design=2000 mm  [stored 6.56168 ft]
- 1000SW-2109XX-1500Pa: Area Left Sash Glazing=0.69 m²; Area Right Sash Glazing=0.69 m²; Clearvue SHGC Value=0.656; Clearvue U Value=6; Custom Windload=1500 mm  [stored 4.92126 ft]; Custom Window Height=890 mm  [stored 2.91995 ft]; Custom Window Width=2090 mm  [stored 6.85696 ft]; Energy Advantage SHGC Value=0.587; Energy Advantage U Value=4.49; Heavy Duty Interlocker=No; Height=890 mm  [stored 2.91995 ft]; Intruderprufe LowE SHGC Value=0.543; Intruderprufe LowE U Value=4.44; Intruderprufe SHGC Value=0.623; Intruderprufe U Value=5.88; Is Heavy Duty Mullion=0 mm  [stored 0 ft]; Limit Sash Width Left Max=1500 mm  [stored 4.92126 ft]; Limit Sash Width Left Min=591 mm; Max Pane Area=0.69 m²; Sash Height=833 mm; Sash Width Left=1046 mm; Sash Width Right=1046 mm; Standard Interlocker=Yes; Width=2090 mm  [stored 6.85696 ft]; Windload Design=1500 mm  [stored 4.92126 ft]
- 1000SW-2109XX-2000Pa: Area Left Sash Glazing=0.69 m²; Area Right Sash Glazing=0.69 m²; Clearvue SHGC Value=0.656; Clearvue U Value=6; Custom Windload=2000 mm  [stored 6.56168 ft]; Custom Window Height=890 mm  [stored 2.91995 ft]; Custom Window Width=2090 mm  [stored 6.85696 ft]; Energy Advantage SHGC Value=0.587; Energy Advantage U Value=4.49; Heavy Duty Interlocker=No; Height=890 mm  [stored 2.91995 ft]; Intruderprufe LowE SHGC Value=0.543; Intruderprufe LowE U Value=4.44; Intruderprufe SHGC Value=0.623; Intruderprufe U Value=5.88; Is Heavy Duty Mullion=0 mm  [stored 0 ft]; Limit Sash Width Left Max=1500 mm  [stored 4.92126 ft]; Limit Sash Width Left Min=591 mm; Max Pane Area=0.69 m²; Sash Height=833 mm; Sash Width Left=1046 mm; Sash Width Right=1046 mm; Standard Interlocker=Yes; Width=2090 mm  [stored 6.85696 ft]; Windload Design=2000 mm  [stored 6.56168 ft]
- 1000SW-2112XX-1500Pa: Area Left Sash Glazing=0.98 m²; Area Right Sash Glazing=0.98 m²; Clearvue SHGC Value=0.693; Clearvue U Value=5.92; Custom Windload=1500 mm  [stored 4.92126 ft]; Custom Window Height=1190 mm  [stored 3.9042 ft]; Custom Window Width=2090 mm  [stored 6.85696 ft]; Energy Advantage SHGC Value=0.62; Energy Advantage U Value=4.32; Heavy Duty Interlocker=No; Height=1190 mm  [stored 3.9042 ft]; Intruderprufe LowE SHGC Value=0.574; Intruderprufe LowE U Value=4.26; Intruderprufe SHGC Value=0.658; Intruderprufe U Value=5.8; Is Heavy Duty Mullion=0 mm  [stored 0 ft]; Limit Sash Width Left Max=1500 mm  [stored 4.92126 ft]; Limit Sash Width Left Min=591 mm; Max Pane Area=0.98 m²; Sash Height=1133 mm; Sash Width Left=1046 mm; Sash Width Right=1046 mm; Standard Interlocker=Yes; Width=2090 mm  [stored 6.85696 ft]; Windload Design=1500 mm  [stored 4.92126 ft]
- 1000SW-2112XX-2000Pa: Area Left Sash Glazing=0.98 m²; Area Right Sash Glazing=0.98 m²; Clearvue SHGC Value=0.693; Clearvue U Value=5.92; Custom Windload=2000 mm  [stored 6.56168 ft]; Custom Window Height=1190 mm  [stored 3.9042 ft]; Custom Window Width=2090 mm  [stored 6.85696 ft]; Energy Advantage SHGC Value=0.62; Energy Advantage U Value=4.32; Heavy Duty Interlocker=No; Height=1190 mm  [stored 3.9042 ft]; Intruderprufe LowE SHGC Value=0.574; Intruderprufe LowE U Value=4.26; Intruderprufe SHGC Value=0.658; Intruderprufe U Value=5.8; Is Heavy Duty Mullion=0 mm  [stored 0 ft]; Limit Sash Width Left Max=1500 mm  [stored 4.92126 ft]; Limit Sash Width Left Min=591 mm; Max Pane Area=0.98 m²; Sash Height=1133 mm; Sash Width Left=1046 mm; Sash Width Right=1046 mm; Standard Interlocker=Yes; Width=2090 mm  [stored 6.85696 ft]; Windload Design=2000 mm  [stored 6.56168 ft]
- 1000SW-2115XX-1500Pa: Area Left Sash Glazing=1.26 m²; Area Right Sash Glazing=1.26 m²; Clearvue SHGC Value=0.715; Clearvue U Value=5.87; Custom Windload=1500 mm  [stored 4.92126 ft]; Custom Window Height=1490 mm  [stored 4.88845 ft]; Custom Window Width=2090 mm  [stored 6.85696 ft]; Energy Advantage SHGC Value=0.639; Energy Advantage U Value=4.21; Heavy Duty Interlocker=Yes; Height=1490 mm  [stored 4.88845 ft]; Intruderprufe LowE SHGC Value=0.595; Intruderprufe LowE U Value=4.15; Intruderprufe SHGC Value=0.679; Intruderprufe U Value=5.75; Is Heavy Duty Mullion=1 mm  [stored 0.00328084 ft]; Limit Sash Width Left Max=1500 mm  [stored 4.92126 ft]; Limit Sash Width Left Min=591 mm; Max Pane Area=1.26 m²; Sash Height=1433 mm; Sash Width Left=1046 mm; Sash Width Right=1046 mm; Standard Interlocker=No; Width=2090 mm  [stored 6.85696 ft]; Windload Design=1500 mm  [stored 4.92126 ft]
- 1000SW-2115XX-2000Pa: Area Left Sash Glazing=1.26 m²; Area Right Sash Glazing=1.26 m²; Clearvue SHGC Value=0.715; Clearvue U Value=5.87; Custom Windload=2000 mm  [stored 6.56168 ft]; Custom Window Height=1490 mm  [stored 4.88845 ft]; Custom Window Width=2090 mm  [stored 6.85696 ft]; Energy Advantage SHGC Value=0.639; Energy Advantage U Value=4.21; Heavy Duty Interlocker=Yes; Height=1490 mm  [stored 4.88845 ft]; Intruderprufe LowE SHGC Value=0.595; Intruderprufe LowE U Value=4.15; Intruderprufe SHGC Value=0.679; Intruderprufe U Value=5.75; Is Heavy Duty Mullion=1 mm  [stored 0.00328084 ft]; Limit Sash Width Left Max=1500 mm  [stored 4.92126 ft]; Limit Sash Width Left Min=591 mm; Max Pane Area=1.26 m²; Sash Height=1433 mm; Sash Width Left=1046 mm; Sash Width Right=1046 mm; Standard Interlocker=No; Width=2090 mm  [stored 6.85696 ft]; Windload Design=2000 mm  [stored 6.56168 ft]
- 1000SW-2118XX-1500Pa: Area Left Sash Glazing=1.54 m²; Area Right Sash Glazing=1.54 m²; Clearvue SHGC Value=0.73; Clearvue U Value=5.83; Custom Windload=1500 mm  [stored 4.92126 ft]; Custom Window Height=1790 mm  [stored 5.8727 ft]; Custom Window Width=2090 mm  [stored 6.85696 ft]; Energy Advantage SHGC Value=0.652; Energy Advantage U Value=4.14; Heavy Duty Interlocker=Yes; Height=1790 mm  [stored 5.8727 ft]; Intruderprufe LowE SHGC Value=0.605; Intruderprufe LowE U Value=4.08; Intruderprufe SHGC Value=0.693; Intruderprufe U Value=5.71; Is Heavy Duty Mullion=1 mm  [stored 0.00328084 ft]; Limit Sash Width Left Max=1500 mm  [stored 4.92126 ft]; Limit Sash Width Left Min=591 mm; Max Pane Area=1.54 m²; Sash Height=1733 mm; Sash Width Left=1046 mm; Sash Width Right=1046 mm; Standard Interlocker=No; Width=2090 mm  [stored 6.85696 ft]; Windload Design=1500 mm  [stored 4.92126 ft]
- 1000SW-2118XX-2000Pa: Area Left Sash Glazing=1.54 m²; Area Right Sash Glazing=1.54 m²; Clearvue SHGC Value=0.73; Clearvue U Value=5.83; Custom Windload=2000 mm  [stored 6.56168 ft]; Custom Window Height=1790 mm  [stored 5.8727 ft]; Custom Window Width=2090 mm  [stored 6.85696 ft]; Energy Advantage SHGC Value=0.652; Energy Advantage U Value=4.14; Heavy Duty Interlocker=Yes; Height=1790 mm  [stored 5.8727 ft]; Intruderprufe LowE SHGC Value=0.605; Intruderprufe LowE U Value=4.08; Intruderprufe SHGC Value=0.693; Intruderprufe U Value=5.71; Is Heavy Duty Mullion=1 mm  [stored 0.00328084 ft]; Limit Sash Width Left Max=1500 mm  [stored 4.92126 ft]; Limit Sash Width Left Min=591 mm; Max Pane Area=1.54 m²; Sash Height=1733 mm; Sash Width Left=1046 mm; Sash Width Right=1046 mm; Standard Interlocker=No; Width=2090 mm  [stored 6.85696 ft]; Windload Design=2000 mm  [stored 6.56168 ft]
- 1000SW-2406XX-1500Pa: Area Left Sash Glazing=0.47 m²; Area Right Sash Glazing=0.47 m²; Clearvue SHGC Value=0.586; Clearvue U Value=6.19; Custom Windload=1500 mm  [stored 4.92126 ft]; Custom Window Height=590 mm  [stored 1.9357 ft]; Custom Window Width=2390 mm  [stored 7.84121 ft]; Energy Advantage SHGC Value=0.525; Energy Advantage U Value=4.84; Heavy Duty Interlocker=No; Height=590 mm  [stored 1.9357 ft]; Intruderprufe LowE SHGC Value=0.484; Intruderprufe LowE U Value=4.8; Intruderprufe SHGC Value=0.556; Intruderprufe U Value=6.08; Is Heavy Duty Mullion=0 mm  [stored 0 ft]; Limit Sash Width Left Max=1500 mm  [stored 4.92126 ft]; Limit Sash Width Left Min=891 mm; Max Pane Area=0.47 m²; Sash Height=533 mm; Sash Width Left=1196 mm; Sash Width Right=1196 mm; Standard Interlocker=Yes; Width=2390 mm  [stored 7.84121 ft]; Windload Design=1500 mm  [stored 4.92126 ft]
- 1000SW-2406XX-2000Pa: Area Left Sash Glazing=0.47 m²; Area Right Sash Glazing=0.47 m²; Clearvue SHGC Value=0.586; Clearvue U Value=6.19; Custom Windload=2000 mm  [stored 6.56168 ft]; Custom Window Height=590 mm  [stored 1.9357 ft]; Custom Window Width=2390 mm  [stored 7.84121 ft]; Energy Advantage SHGC Value=0.525; Energy Advantage U Value=4.84; Heavy Duty Interlocker=No; Height=590 mm  [stored 1.9357 ft]; Intruderprufe LowE SHGC Value=0.484; Intruderprufe LowE U Value=4.8; Intruderprufe SHGC Value=0.556; Intruderprufe U Value=6.08; Is Heavy Duty Mullion=0 mm  [stored 0 ft]; Limit Sash Width Left Max=1500 mm  [stored 4.92126 ft]; Limit Sash Width Left Min=891 mm; Max Pane Area=0.47 m²; Sash Height=533 mm; Sash Width Left=1196 mm; Sash Width Right=1196 mm; Standard Interlocker=Yes; Width=2390 mm  [stored 7.84121 ft]; Windload Design=2000 mm  [stored 6.56168 ft]
- 1000SW-2409XX-1500Pa: Area Left Sash Glazing=0.8 m²; Area Right Sash Glazing=0.8 m²; Clearvue SHGC Value=0.661; Clearvue U Value=6.02; Custom Windload=1500 mm  [stored 4.92126 ft]; Custom Window Height=890 mm  [stored 2.91995 ft]; Custom Window Width=2390 mm  [stored 7.84121 ft]; Energy Advantage SHGC Value=0.591; Energy Advantage U Value=4.48; Heavy Duty Interlocker=No; Height=890 mm  [stored 2.91995 ft]; Intruderprufe LowE SHGC Value=0.547; Intruderprufe LowE U Value=4.44; Intruderprufe SHGC Value=0.627; Intruderprufe U Value=5.91; Is Heavy Duty Mullion=0 mm  [stored 0 ft]; Limit Sash Width Left Max=1500 mm  [stored 4.92126 ft]; Limit Sash Width Left Min=891 mm; Max Pane Area=0.8 m²; Sash Height=833 mm; Sash Width Left=1196 mm; Sash Width Right=1196 mm; Standard Interlocker=Yes; Width=2390 mm  [stored 7.84121 ft]; Windload Design=1500 mm  [stored 4.92126 ft]
- 1000SW-2409XX-2000Pa: Area Left Sash Glazing=0.8 m²; Area Right Sash Glazing=0.8 m²; Clearvue SHGC Value=0.661; Clearvue U Value=6.02; Custom Windload=2000 mm  [stored 6.56168 ft]; Custom Window Height=890 mm  [stored 2.91995 ft]; Custom Window Width=2390 mm  [stored 7.84121 ft]; Energy Advantage SHGC Value=0.591; Energy Advantage U Value=4.48; Heavy Duty Interlocker=No; Height=890 mm  [stored 2.91995 ft]; Intruderprufe LowE SHGC Value=0.547; Intruderprufe LowE U Value=4.44; Intruderprufe SHGC Value=0.627; Intruderprufe U Value=5.91; Is Heavy Duty Mullion=0 mm  [stored 0 ft]; Limit Sash Width Left Max=1500 mm  [stored 4.92126 ft]; Limit Sash Width Left Min=891 mm; Max Pane Area=0.8 m²; Sash Height=833 mm; Sash Width Left=1196 mm; Sash Width Right=1196 mm; Standard Interlocker=Yes; Width=2390 mm  [stored 7.84121 ft]; Windload Design=2000 mm  [stored 6.56168 ft]
- 1000SW-2412XX-1500Pa: Area Left Sash Glazing=1.13 m²; Area Right Sash Glazing=1.13 m²; Clearvue SHGC Value=0.698; Clearvue U Value=5.94; Custom Windload=1500 mm  [stored 4.92126 ft]; Custom Window Height=1190 mm  [stored 3.9042 ft]; Custom Window Width=2390 mm  [stored 7.84121 ft]; Energy Advantage SHGC Value=0.624; Energy Advantage U Value=4.31; Heavy Duty Interlocker=No; Height=1190 mm  [stored 3.9042 ft]; Intruderprufe LowE SHGC Value=0.578; Intruderprufe LowE U Value=4.26; Intruderprufe SHGC Value=0.663; Intruderprufe U Value=5.82; Is Heavy Duty Mullion=0 mm  [stored 0 ft]; Limit Sash Width Left Max=1500 mm  [stored 4.92126 ft]; Limit Sash Width Left Min=891 mm; Max Pane Area=1.13 m²; Sash Height=1133 mm; Sash Width Left=1196 mm; Sash Width Right=1196 mm; Standard Interlocker=Yes; Width=2390 mm  [stored 7.84121 ft]; Windload Design=1500 mm  [stored 4.92126 ft]
- 1000SW-2412XX-2000Pa: Area Left Sash Glazing=1.13 m²; Area Right Sash Glazing=1.13 m²; Clearvue SHGC Value=0.698; Clearvue U Value=5.94; Custom Windload=2000 mm  [stored 6.56168 ft]; Custom Window Height=1190 mm  [stored 3.9042 ft]; Custom Window Width=2390 mm  [stored 7.84121 ft]; Energy Advantage SHGC Value=0.624; Energy Advantage U Value=4.31; Heavy Duty Interlocker=No; Height=1190 mm  [stored 3.9042 ft]; Intruderprufe LowE SHGC Value=0.578; Intruderprufe LowE U Value=4.26; Intruderprufe SHGC Value=0.663; Intruderprufe U Value=5.82; Is Heavy Duty Mullion=0 mm  [stored 0 ft]; Limit Sash Width Left Max=1500 mm  [stored 4.92126 ft]; Limit Sash Width Left Min=891 mm; Max Pane Area=1.13 m²; Sash Height=1133 mm; Sash Width Left=1196 mm; Sash Width Right=1196 mm; Standard Interlocker=Yes; Width=2390 mm  [stored 7.84121 ft]; Windload Design=2000 mm  [stored 6.56168 ft]
- 1000SW-2415XX-1500Pa: Area Left Sash Glazing=1.46 m²; Area Right Sash Glazing=1.46 m²; Clearvue SHGC Value=0.721; Clearvue U Value=5.89; Custom Windload=1500 mm  [stored 4.92126 ft]; Custom Window Height=1490 mm  [stored 4.88845 ft]; Custom Window Width=2390 mm  [stored 7.84121 ft]; Energy Advantage SHGC Value=0.644; Energy Advantage U Value=4.2; Heavy Duty Interlocker=Yes; Height=1490 mm  [stored 4.88845 ft]; Intruderprufe LowE SHGC Value=0.597; Intruderprufe LowE U Value=4.15; Intruderprufe SHGC Value=0.684; Intruderprufe U Value=5.77; Is Heavy Duty Mullion=1 mm  [stored 0.00328084 ft]; Limit Sash Width Left Max=1500 mm  [stored 4.92126 ft]; Limit Sash Width Left Min=891 mm; Max Pane Area=1.46 m²; Sash Height=1433 mm; Sash Width Left=1196 mm; Sash Width Right=1196 mm; Standard Interlocker=No; Width=2390 mm  [stored 7.84121 ft]; Windload Design=1500 mm  [stored 4.92126 ft]
- 1000SW-2415XX-2000Pa: Area Left Sash Glazing=1.46 m²; Area Right Sash Glazing=1.46 m²; Clearvue SHGC Value=0.721; Clearvue U Value=5.89; Custom Windload=2000 mm  [stored 6.56168 ft]; Custom Window Height=1490 mm  [stored 4.88845 ft]; Custom Window Width=2390 mm  [stored 7.84121 ft]; Energy Advantage SHGC Value=0.644; Energy Advantage U Value=4.2; Heavy Duty Interlocker=Yes; Height=1490 mm  [stored 4.88845 ft]; Intruderprufe LowE SHGC Value=0.597; Intruderprufe LowE U Value=4.15; Intruderprufe SHGC Value=0.684; Intruderprufe U Value=5.77; Is Heavy Duty Mullion=1 mm  [stored 0.00328084 ft]; Limit Sash Width Left Max=1500 mm  [stored 4.92126 ft]; Limit Sash Width Left Min=891 mm; Max Pane Area=1.46 m²; Sash Height=1433 mm; Sash Width Left=1196 mm; Sash Width Right=1196 mm; Standard Interlocker=No; Width=2390 mm  [stored 7.84121 ft]; Windload Design=2000 mm  [stored 6.56168 ft]
- 1000SW-2418XX-1500Pa: Area Left Sash Glazing=1.79 m²; Area Right Sash Glazing=1.79 m²; Clearvue SHGC Value=0.735; Clearvue U Value=5.86; Custom Windload=1500 mm  [stored 4.92126 ft]; Custom Window Height=1790 mm  [stored 5.8727 ft]; Custom Window Width=2390 mm  [stored 7.84121 ft]; Energy Advantage SHGC Value=0.657; Energy Advantage U Value=4.13; Heavy Duty Interlocker=Yes; Height=1790 mm  [stored 5.8727 ft]; Intruderprufe LowE SHGC Value=0.61; Intruderprufe LowE U Value=4.07; Intruderprufe SHGC Value=0.698; Intruderprufe U Value=5.74; Is Heavy Duty Mullion=1 mm  [stored 0.00328084 ft]; Limit Sash Width Left Max=1500 mm  [stored 4.92126 ft]; Limit Sash Width Left Min=891 mm; Max Pane Area=1.79 m²; Sash Height=1733 mm; Sash Width Left=1196 mm; Sash Width Right=1196 mm; Standard Interlocker=No; Width=2390 mm  [stored 7.84121 ft]; Windload Design=1500 mm  [stored 4.92126 ft]
- 1000SW-2418XX-2000Pa: Area Left Sash Glazing=1.79 m²; Area Right Sash Glazing=1.79 m²; Clearvue SHGC Value=0.735; Clearvue U Value=5.86; Custom Windload=2000 mm  [stored 6.56168 ft]; Custom Window Height=1790 mm  [stored 5.8727 ft]; Custom Window Width=2390 mm  [stored 7.84121 ft]; Energy Advantage SHGC Value=0.657; Energy Advantage U Value=4.13; Heavy Duty Interlocker=Yes; Height=1790 mm  [stored 5.8727 ft]; Intruderprufe LowE SHGC Value=0.61; Intruderprufe LowE U Value=4.07; Intruderprufe SHGC Value=0.698; Intruderprufe U Value=5.74; Is Heavy Duty Mullion=1 mm  [stored 0.00328084 ft]; Limit Sash Width Left Max=1500 mm  [stored 4.92126 ft]; Limit Sash Width Left Min=891 mm; Max Pane Area=1.79 m²; Sash Height=1733 mm; Sash Width Left=1196 mm; Sash Width Right=1196 mm; Standard Interlocker=No; Width=2390 mm  [stored 7.84121 ft]; Windload Design=2000 mm  [stored 6.56168 ft]
- 1000SW-2706XX-1500Pa: Area Left Sash Glazing=0.54 m²; Area Right Sash Glazing=0.54 m²; Clearvue SHGC Value=0.589; Clearvue U Value=6.21; Custom Windload=1500 mm  [stored 4.92126 ft]; Custom Window Height=590 mm  [stored 1.9357 ft]; Custom Window Width=2690 mm; Energy Advantage SHGC Value=0.528; Energy Advantage U Value=4.84; Heavy Duty Interlocker=No; Height=590 mm  [stored 1.9357 ft]; Intruderprufe LowE SHGC Value=0.486; Intruderprufe LowE U Value=4.8; Intruderprufe SHGC Value=0.559; Intruderprufe U Value=6.09; Is Heavy Duty Mullion=0 mm  [stored 0 ft]; Limit Sash Width Left Max=1500 mm  [stored 4.92126 ft]; Limit Sash Width Left Min=1191 mm; Max Pane Area=0.54 m²; Sash Height=533 mm; Sash Width Left=1346 mm; Sash Width Right=1346 mm; Standard Interlocker=Yes; Width=2690 mm; Windload Design=1500 mm  [stored 4.92126 ft]
- 1000SW-2706XX-2000Pa: Area Left Sash Glazing=0.54 m²; Area Right Sash Glazing=0.54 m²; Clearvue SHGC Value=0.589; Clearvue U Value=6.21; Custom Windload=2000 mm  [stored 6.56168 ft]; Custom Window Height=590 mm  [stored 1.9357 ft]; Custom Window Width=2690 mm; Energy Advantage SHGC Value=0.528; Energy Advantage U Value=4.84; Heavy Duty Interlocker=No; Height=590 mm  [stored 1.9357 ft]; Intruderprufe LowE SHGC Value=0.486; Intruderprufe LowE U Value=4.8; Intruderprufe SHGC Value=0.559; Intruderprufe U Value=6.09; Is Heavy Duty Mullion=0 mm  [stored 0 ft]; Limit Sash Width Left Max=1500 mm  [stored 4.92126 ft]; Limit Sash Width Left Min=1191 mm; Max Pane Area=0.54 m²; Sash Height=533 mm; Sash Width Left=1346 mm; Sash Width Right=1346 mm; Standard Interlocker=Yes; Width=2690 mm; Windload Design=2000 mm  [stored 6.56168 ft]
- 1000SW-2709XX-1500Pa: Area Left Sash Glazing=0.91 m²; Area Right Sash Glazing=0.91 m²; Clearvue SHGC Value=0.665; Clearvue U Value=6.04; Custom Windload=1500 mm  [stored 4.92126 ft]; Custom Window Height=890 mm  [stored 2.91995 ft]; Custom Window Width=2690 mm; Energy Advantage SHGC Value=0.595; Energy Advantage U Value=4.48; Heavy Duty Interlocker=No; Height=890 mm  [stored 2.91995 ft]; Intruderprufe LowE SHGC Value=0.55; Intruderprufe LowE U Value=4.43; Intruderprufe SHGC Value=0.631; Intruderprufe U Value=5.92; Is Heavy Duty Mullion=0 mm  [stored 0 ft]; Limit Sash Width Left Max=1500 mm  [stored 4.92126 ft]; Limit Sash Width Left Min=1191 mm; Max Pane Area=0.91 m²; Sash Height=833 mm; Sash Width Left=1346 mm; Sash Width Right=1346 mm; Standard Interlocker=Yes; Width=2690 mm; Windload Design=1500 mm  [stored 4.92126 ft]
- 1000SW-2709XX-2000Pa: Area Left Sash Glazing=0.91 m²; Area Right Sash Glazing=0.91 m²; Clearvue SHGC Value=0.665; Clearvue U Value=6.04; Custom Windload=2000 mm  [stored 6.56168 ft]; Custom Window Height=890 mm  [stored 2.91995 ft]; Custom Window Width=2690 mm; Energy Advantage SHGC Value=0.595; Energy Advantage U Value=4.48; Heavy Duty Interlocker=No; Height=890 mm  [stored 2.91995 ft]; Intruderprufe LowE SHGC Value=0.55; Intruderprufe LowE U Value=4.43; Intruderprufe SHGC Value=0.631; Intruderprufe U Value=5.92; Is Heavy Duty Mullion=0 mm  [stored 0 ft]; Limit Sash Width Left Max=1500 mm  [stored 4.92126 ft]; Limit Sash Width Left Min=1191 mm; Max Pane Area=0.91 m²; Sash Height=833 mm; Sash Width Left=1346 mm; Sash Width Right=1346 mm; Standard Interlocker=Yes; Width=2690 mm; Windload Design=2000 mm  [stored 6.56168 ft]
- 1000SW-2712XX-2000Pa: Area Left Sash Glazing=1.28 m²; Area Right Sash Glazing=1.28 m²; Clearvue SHGC Value=0.702; Clearvue U Value=5.96; Custom Windload=2000 mm  [stored 6.56168 ft]; Custom Window Height=1190 mm  [stored 3.9042 ft]; Custom Window Width=2690 mm; Energy Advantage SHGC Value=0.628; Energy Advantage U Value=4.3; Heavy Duty Interlocker=No; Height=1190 mm  [stored 3.9042 ft]; Intruderprufe LowE SHGC Value=0.582; Intruderprufe LowE U Value=4.25; Intruderprufe SHGC Value=0.666; Intruderprufe U Value=5.84; Is Heavy Duty Mullion=0 mm  [stored 0 ft]; Limit Sash Width Left Max=1500 mm  [stored 4.92126 ft]; Limit Sash Width Left Min=1191 mm; Max Pane Area=1.28 m²; Sash Height=1133 mm; Sash Width Left=1346 mm; Sash Width Right=1346 mm; Standard Interlocker=Yes; Width=2690 mm; Windload Design=2000 mm  [stored 6.56168 ft]
- 1000SW-2715XX-1500Pa: Area Left Sash Glazing=1.66 m²; Area Right Sash Glazing=1.66 m²; Clearvue SHGC Value=0.725; Clearvue U Value=5.91; Custom Windload=1500 mm  [stored 4.92126 ft]; Custom Window Height=1490 mm  [stored 4.88845 ft]; Custom Window Width=2690 mm; Energy Advantage SHGC Value=0.648; Energy Advantage U Value=4.2; Heavy Duty Interlocker=Yes; Height=1490 mm  [stored 4.88845 ft]; Intruderprufe LowE SHGC Value=0.601; Intruderprufe LowE U Value=4.14; Intruderprufe SHGC Value=0.687; Intruderprufe U Value=5.79; Is Heavy Duty Mullion=1 mm  [stored 0.00328084 ft]; Limit Sash Width Left Max=1500 mm  [stored 4.92126 ft]; Limit Sash Width Left Min=1191 mm; Max Pane Area=1.66 m²; Sash Height=1433 mm; Sash Width Left=1346 mm; Sash Width Right=1346 mm; Standard Interlocker=No; Width=2690 mm; Windload Design=1500 mm  [stored 4.92126 ft]
- 1000SW-2715XX-2000Pa: Area Left Sash Glazing=1.66 m²; Area Right Sash Glazing=1.66 m²; Clearvue SHGC Value=0.725; Clearvue U Value=5.91; Custom Windload=2000 mm  [stored 6.56168 ft]; Custom Window Height=1490 mm  [stored 4.88845 ft]; Custom Window Width=2690 mm; Energy Advantage SHGC Value=0.648; Energy Advantage U Value=4.2; Heavy Duty Interlocker=Yes; Height=1490 mm  [stored 4.88845 ft]; Intruderprufe LowE SHGC Value=0.601; Intruderprufe LowE U Value=4.14; Intruderprufe SHGC Value=0.687; Intruderprufe U Value=5.79; Is Heavy Duty Mullion=1 mm  [stored 0.00328084 ft]; Limit Sash Width Left Max=1500 mm  [stored 4.92126 ft]; Limit Sash Width Left Min=1191 mm; Max Pane Area=1.66 m²; Sash Height=1433 mm; Sash Width Left=1346 mm; Sash Width Right=1346 mm; Standard Interlocker=No; Width=2690 mm; Windload Design=2000 mm  [stored 6.56168 ft]
- 1000SW-2718XX-1500Pa: Area Left Sash Glazing=2.03 m²; Area Right Sash Glazing=2.03 m²; Clearvue SHGC Value=0.74; Clearvue U Value=5.88; Custom Windload=1500 mm  [stored 4.92126 ft]; Custom Window Height=1790 mm  [stored 5.8727 ft]; Custom Window Width=2690 mm; Energy Advantage SHGC Value=0.661; Energy Advantage U Value=4.13; Heavy Duty Interlocker=Yes; Height=1790 mm  [stored 5.8727 ft]; Intruderprufe LowE SHGC Value=0.613; Intruderprufe LowE U Value=4.07; Intruderprufe SHGC Value=0.702; Intruderprufe U Value=5.76; Is Heavy Duty Mullion=1 mm  [stored 0.00328084 ft]; Limit Sash Width Left Max=1500 mm  [stored 4.92126 ft]; Limit Sash Width Left Min=1191 mm; Max Pane Area=2.03 m²; Sash Height=1733 mm; Sash Width Left=1346 mm; Sash Width Right=1346 mm; Standard Interlocker=No; Width=2690 mm; Windload Design=1500 mm  [stored 4.92126 ft]
- 1000SW-2718XX-2000Pa: Area Left Sash Glazing=2.03 m²; Area Right Sash Glazing=2.03 m²; Clearvue SHGC Value=0.74; Clearvue U Value=5.88; Custom Windload=2000 mm  [stored 6.56168 ft]; Custom Window Height=1790 mm  [stored 5.8727 ft]; Custom Window Width=2690 mm; Energy Advantage SHGC Value=0.661; Energy Advantage U Value=4.13; Heavy Duty Interlocker=Yes; Height=1790 mm  [stored 5.8727 ft]; Intruderprufe LowE SHGC Value=0.613; Intruderprufe LowE U Value=4.07; Intruderprufe SHGC Value=0.702; Intruderprufe U Value=5.76; Is Heavy Duty Mullion=1 mm  [stored 0.00328084 ft]; Limit Sash Width Left Max=1500 mm  [stored 4.92126 ft]; Limit Sash Width Left Min=1191 mm; Max Pane Area=2.03 m²; Sash Height=1733 mm; Sash Width Left=1346 mm; Sash Width Right=1346 mm; Standard Interlocker=No; Width=2690 mm; Windload Design=2000 mm  [stored 6.56168 ft]
- 1000SW-3006XX-1500Pa: Area Left Sash Glazing=0.6 m²; Area Right Sash Glazing=0.6 m²; Clearvue SHGC Value=0.592; Clearvue U Value=6.22; Custom Windload=1500 mm  [stored 4.92126 ft]; Custom Window Height=590 mm  [stored 1.9357 ft]; Custom Window Width=2990 mm  [stored 9.80971 ft]; Energy Advantage SHGC Value=0.53; Energy Advantage U Value=4.84; Heavy Duty Interlocker=No; Height=590 mm  [stored 1.9357 ft]; Intruderprufe LowE SHGC Value=0.488; Intruderprufe LowE U Value=4.8; Intruderprufe SHGC Value=0.562; Intruderprufe U Value=6.11; Is Heavy Duty Mullion=0 mm  [stored 0 ft]; Limit Sash Width Left Max=1500 mm  [stored 4.92126 ft]; Limit Sash Width Left Min=1491 mm; Max Pane Area=0.6 m²; Sash Height=533 mm; Sash Width Left=1496 mm; Sash Width Right=1496 mm; Standard Interlocker=Yes; Width=2990 mm  [stored 9.80971 ft]; Windload Design=1500 mm  [stored 4.92126 ft]
- 1000SW-3006XX-2000Pa: Area Left Sash Glazing=0.6 m²; Area Right Sash Glazing=0.6 m²; Clearvue SHGC Value=0.592; Clearvue U Value=6.22; Custom Windload=2000 mm  [stored 6.56168 ft]; Custom Window Height=590 mm  [stored 1.9357 ft]; Custom Window Width=2990 mm  [stored 9.80971 ft]; Energy Advantage SHGC Value=0.53; Energy Advantage U Value=4.84; Heavy Duty Interlocker=No; Height=590 mm  [stored 1.9357 ft]; Intruderprufe LowE SHGC Value=0.488; Intruderprufe LowE U Value=4.8; Intruderprufe SHGC Value=0.562; Intruderprufe U Value=6.11; Is Heavy Duty Mullion=0 mm  [stored 0 ft]; Limit Sash Width Left Max=1500 mm  [stored 4.92126 ft]; Limit Sash Width Left Min=1491 mm; Max Pane Area=0.6 m²; Sash Height=533 mm; Sash Width Left=1496 mm; Sash Width Right=1496 mm; Standard Interlocker=Yes; Width=2990 mm  [stored 9.80971 ft]; Windload Design=2000 mm  [stored 6.56168 ft]
- 1000SW-3009XX-1500Pa: Area Left Sash Glazing=1.02 m²; Area Right Sash Glazing=1.02 m²; Clearvue SHGC Value=0.668; Clearvue U Value=6.06; Custom Windload=1500 mm  [stored 4.92126 ft]; Custom Window Height=890 mm  [stored 2.91995 ft]; Custom Window Width=2990 mm  [stored 9.80971 ft]; Energy Advantage SHGC Value=0.597; Energy Advantage U Value=4.48; Heavy Duty Interlocker=No; Height=890 mm  [stored 2.91995 ft]; Intruderprufe LowE SHGC Value=0.552; Intruderprufe LowE U Value=4.43; Intruderprufe SHGC Value=0.634; Intruderprufe U Value=5.94; Is Heavy Duty Mullion=0 mm  [stored 0 ft]; Limit Sash Width Left Max=1500 mm  [stored 4.92126 ft]; Limit Sash Width Left Min=1491 mm; Max Pane Area=1.02 m²; Sash Height=833 mm; Sash Width Left=1496 mm; Sash Width Right=1496 mm; Standard Interlocker=Yes; Width=2990 mm  [stored 9.80971 ft]; Windload Design=1500 mm  [stored 4.92126 ft]
- 1000SW-3009XX-2000Pa: Area Left Sash Glazing=1.02 m²; Area Right Sash Glazing=1.02 m²; Clearvue SHGC Value=0.668; Clearvue U Value=6.06; Custom Windload=2000 mm  [stored 6.56168 ft]; Custom Window Height=890 mm  [stored 2.91995 ft]; Custom Window Width=2990 mm  [stored 9.80971 ft]; Energy Advantage SHGC Value=0.597; Energy Advantage U Value=4.48; Heavy Duty Interlocker=No; Height=890 mm  [stored 2.91995 ft]; Intruderprufe LowE SHGC Value=0.552; Intruderprufe LowE U Value=4.43; Intruderprufe SHGC Value=0.634; Intruderprufe U Value=5.94; Is Heavy Duty Mullion=0 mm  [stored 0 ft]; Limit Sash Width Left Max=1500 mm  [stored 4.92126 ft]; Limit Sash Width Left Min=1491 mm; Max Pane Area=1.02 m²; Sash Height=833 mm; Sash Width Left=1496 mm; Sash Width Right=1496 mm; Standard Interlocker=Yes; Width=2990 mm  [stored 9.80971 ft]; Windload Design=2000 mm  [stored 6.56168 ft]
- 1000SW-3012XX-1500Pa: Area Left Sash Glazing=1.44 m²; Area Right Sash Glazing=1.44 m²; Clearvue SHGC Value=0.705; Clearvue U Value=5.98; Custom Windload=1500 mm  [stored 4.92126 ft]; Custom Window Height=1190 mm  [stored 3.9042 ft]; Custom Window Width=2990 mm  [stored 9.80971 ft]; Energy Advantage SHGC Value=0.631; Energy Advantage U Value=4.3; Heavy Duty Interlocker=No; Height=1190 mm  [stored 3.9042 ft]; Intruderprufe LowE SHGC Value=0.584; Intruderprufe LowE U Value=4.25; Intruderprufe SHGC Value=0.669; Intruderprufe U Value=5.86; Is Heavy Duty Mullion=0 mm  [stored 0 ft]; Limit Sash Width Left Max=1500 mm  [stored 4.92126 ft]; Limit Sash Width Left Min=1491 mm; Max Pane Area=1.44 m²; Sash Height=1133 mm; Sash Width Left=1496 mm; Sash Width Right=1496 mm; Standard Interlocker=Yes; Width=2990 mm  [stored 9.80971 ft]; Windload Design=1500 mm  [stored 4.92126 ft]
- 1000SW-3012XX-2000Pa: Area Left Sash Glazing=1.44 m²; Area Right Sash Glazing=1.44 m²; Clearvue SHGC Value=0.705; Clearvue U Value=5.98; Custom Windload=2000 mm  [stored 6.56168 ft]; Custom Window Height=1190 mm  [stored 3.9042 ft]; Custom Window Width=2990 mm  [stored 9.80971 ft]; Energy Advantage SHGC Value=0.631; Energy Advantage U Value=4.3; Heavy Duty Interlocker=No; Height=1190 mm  [stored 3.9042 ft]; Intruderprufe LowE SHGC Value=0.584; Intruderprufe LowE U Value=4.25; Intruderprufe SHGC Value=0.669; Intruderprufe U Value=5.86; Is Heavy Duty Mullion=0 mm  [stored 0 ft]; Limit Sash Width Left Max=1500 mm  [stored 4.92126 ft]; Limit Sash Width Left Min=1491 mm; Max Pane Area=1.44 m²; Sash Height=1133 mm; Sash Width Left=1496 mm; Sash Width Right=1496 mm; Standard Interlocker=Yes; Width=2990 mm  [stored 9.80971 ft]; Windload Design=2000 mm  [stored 6.56168 ft]
- 1000SW-3015XX-1500Pa: Area Left Sash Glazing=1.86 m²; Area Right Sash Glazing=1.86 m²; Clearvue SHGC Value=0.728; Clearvue U Value=5.93; Custom Windload=1500 mm  [stored 4.92126 ft]; Custom Window Height=1490 mm  [stored 4.88845 ft]; Custom Window Width=2990 mm  [stored 9.80971 ft]; Energy Advantage SHGC Value=0.651; Energy Advantage U Value=4.19; Heavy Duty Interlocker=Yes; Height=1490 mm  [stored 4.88845 ft]; Intruderprufe LowE SHGC Value=0.603; Intruderprufe LowE U Value=4.14; Intruderprufe SHGC Value=0.691; Intruderprufe U Value=5.81; Is Heavy Duty Mullion=1 mm  [stored 0.00328084 ft]; Limit Sash Width Left Max=1500 mm  [stored 4.92126 ft]; Limit Sash Width Left Min=1491 mm; Max Pane Area=1.86 m²; Sash Height=1433 mm; Sash Width Left=1496 mm; Sash Width Right=1496 mm; Standard Interlocker=No; Width=2990 mm  [stored 9.80971 ft]; Windload Design=1500 mm  [stored 4.92126 ft]
- 1000SW-3015XX-2000Pa: Area Left Sash Glazing=1.86 m²; Area Right Sash Glazing=1.86 m²; Clearvue SHGC Value=0.728; Clearvue U Value=5.93; Custom Windload=2000 mm  [stored 6.56168 ft]; Custom Window Height=1490 mm  [stored 4.88845 ft]; Custom Window Width=2990 mm  [stored 9.80971 ft]; Energy Advantage SHGC Value=0.651; Energy Advantage U Value=4.19; Heavy Duty Interlocker=Yes; Height=1490 mm  [stored 4.88845 ft]; Intruderprufe LowE SHGC Value=0.603; Intruderprufe LowE U Value=4.14; Intruderprufe SHGC Value=0.691; Intruderprufe U Value=5.81; Is Heavy Duty Mullion=1 mm  [stored 0.00328084 ft]; Limit Sash Width Left Max=1500 mm  [stored 4.92126 ft]; Limit Sash Width Left Min=1491 mm; Max Pane Area=1.86 m²; Sash Height=1433 mm; Sash Width Left=1496 mm; Sash Width Right=1496 mm; Standard Interlocker=No; Width=2990 mm  [stored 9.80971 ft]; Windload Design=2000 mm  [stored 6.56168 ft]
- 1000SW-3018XX-2000Pa: Area Left Sash Glazing=2.28 m²; Area Right Sash Glazing=2.28 m²; Clearvue SHGC Value=0.743; Clearvue U Value=5.9; Custom Windload=2000 mm  [stored 6.56168 ft]; Custom Window Height=1790 mm  [stored 5.8727 ft]; Custom Window Width=2990 mm  [stored 9.80971 ft]; Energy Advantage SHGC Value=0.664; Energy Advantage U Value=4.12; Heavy Duty Interlocker=Yes; Height=1790 mm  [stored 5.8727 ft]; Intruderprufe LowE SHGC Value=0.616; Intruderprufe LowE U Value=4.06; Intruderprufe SHGC Value=0.705; Intruderprufe U Value=5.77; Is Heavy Duty Mullion=1 mm  [stored 0.00328084 ft]; Limit Sash Width Left Max=1500 mm  [stored 4.92126 ft]; Limit Sash Width Left Min=1491 mm; Max Pane Area=2.28 m²; Sash Height=1733 mm; Sash Width Left=1496 mm; Sash Width Right=1496 mm; Standard Interlocker=No; Width=2990 mm  [stored 9.80971 ft]; Windload Design=2000 mm  [stored 6.56168 ft]
- 1000SW-3018XX-1500Pa: Area Left Sash Glazing=2.28 m²; Area Right Sash Glazing=2.28 m²; Clearvue SHGC Value=0.743; Clearvue U Value=5.9; Custom Windload=1500 mm  [stored 4.92126 ft]; Custom Window Height=1790 mm  [stored 5.8727 ft]; Custom Window Width=2990 mm  [stored 9.80971 ft]; Energy Advantage SHGC Value=0.664; Energy Advantage U Value=4.12; Heavy Duty Interlocker=Yes; Height=1790 mm  [stored 5.8727 ft]; Intruderprufe LowE SHGC Value=0.616; Intruderprufe LowE U Value=4.06; Intruderprufe SHGC Value=0.705; Intruderprufe U Value=5.77; Is Heavy Duty Mullion=1 mm  [stored 0.00328084 ft]; Limit Sash Width Left Max=1500 mm  [stored 4.92126 ft]; Limit Sash Width Left Min=1491 mm; Max Pane Area=2.28 m²; Sash Height=1733 mm; Sash Width Left=1496 mm; Sash Width Right=1496 mm; Standard Interlocker=No; Width=2990 mm  [stored 9.80971 ft]; Windload Design=1500 mm  [stored 4.92126 ft]
- 1000SW-2712XX-1500Pa: Area Left Sash Glazing=1.28 m²; Area Right Sash Glazing=1.28 m²; Clearvue SHGC Value=0.702; Clearvue U Value=5.96; Custom Windload=1500 mm  [stored 4.92126 ft]; Custom Window Height=1190 mm  [stored 3.9042 ft]; Custom Window Width=2690 mm; Energy Advantage SHGC Value=0.628; Energy Advantage U Value=4.3; Heavy Duty Interlocker=No; Height=1190 mm  [stored 3.9042 ft]; Intruderprufe LowE SHGC Value=0.582; Intruderprufe LowE U Value=4.25; Intruderprufe SHGC Value=0.666; Intruderprufe U Value=5.84; Is Heavy Duty Mullion=0 mm  [stored 0 ft]; Limit Sash Width Left Max=1500 mm  [stored 4.92126 ft]; Limit Sash Width Left Min=1191 mm; Max Pane Area=1.28 m²; Sash Height=1133 mm; Sash Width Left=1346 mm; Sash Width Right=1346 mm; Standard Interlocker=Yes; Width=2690 mm; Windload Design=1500 mm  [stored 4.92126 ft]

note: [stored X ft] marks values corroborated as IEEE doubles in the binary element streams (Revit-internal decimal feet)

## geometry (parser evidence)
native form markers: Sweep x11
no freeform markers — native parametric forms only
